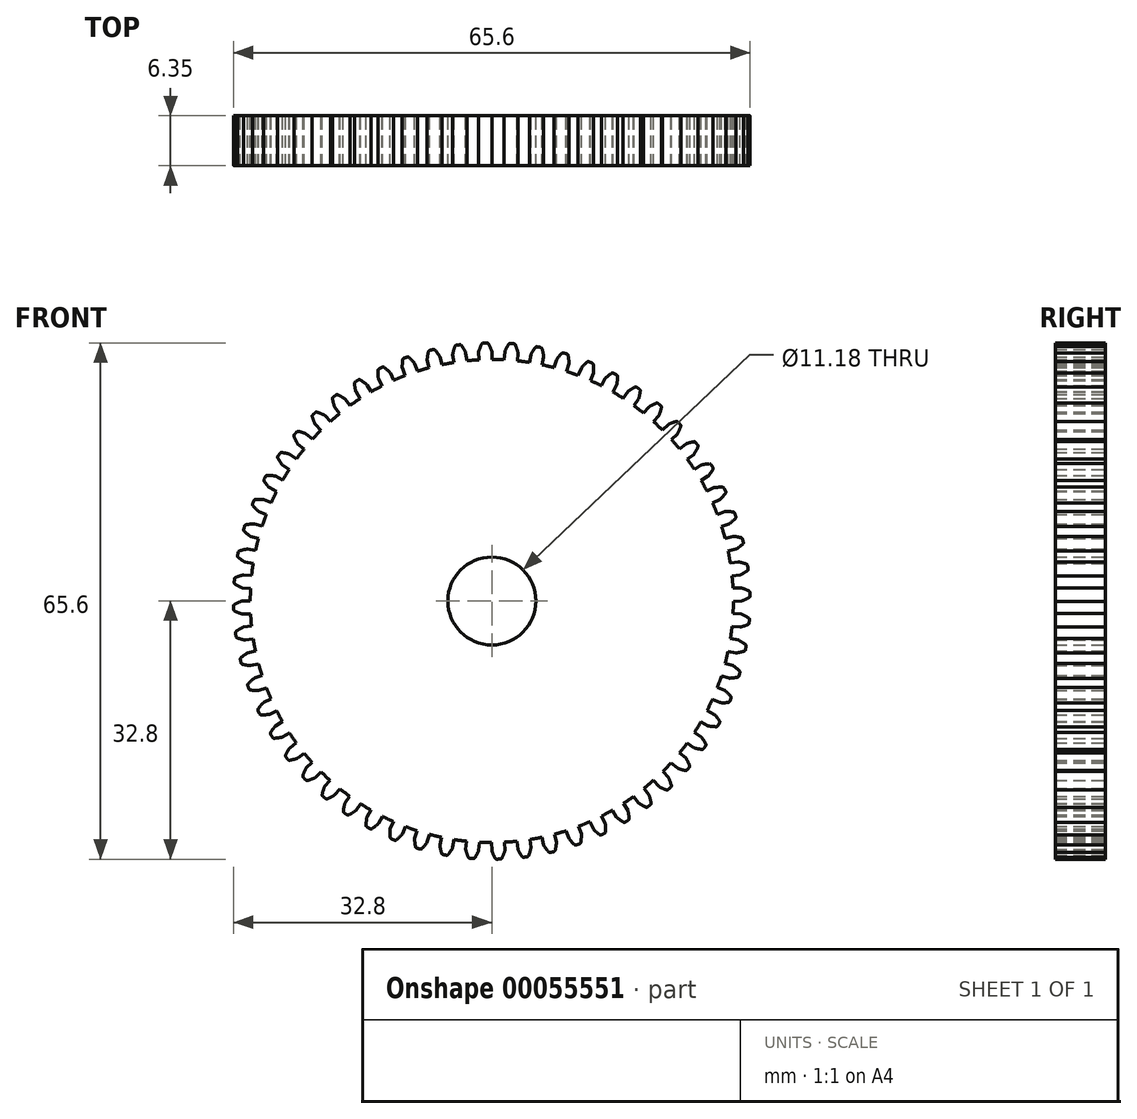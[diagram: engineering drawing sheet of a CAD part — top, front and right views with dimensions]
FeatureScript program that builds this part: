
annotation { "Feature Type Name" : "Feature", "Feature Type Description" : "" }
export const myFeature = defineFeature(function(context is Context, id is Id, definition is map)
    precondition{}
    {
        {
            var Q0;
            Q0=qCreatedBy(makeId("Front.planeOp"),FACE);
            var sketch = newSketch(context, id + "F0", { "sketchPlane" : qUnion([Q0])});
            skCircle(sketch, "E0", {"center": v(0, 0) * mm, "radius": 30.68 * mm});
            skArc(sketch, "E1", {"start": v(-0.65, 32.8) * mm, "mid": v(-0.75, 32.8) * mm, "end": v(-0.86, 32.8) * mm});
            skLineSegment(sketch, "E2", {"start": v(-1.25, 23.9) * mm, "end": v(-1.25, 23.91) * mm, "construction": true});
            skArc(sketch, "E3.trimOffspring", {"start": v(-0.02, 31.8) * mm, "mid": v(-0.2, 32.23) * mm, "end": v(-0.42, 32.66) * mm});
            skLineSegment(sketch, "E4", {"start": v(0, 31.7) * mm, "end": v(0.03, 30.68) * mm});
            skLineSegment(sketch, "E5.MirrorCS", {"start": v(-1.66, 31.66) * mm, "end": v(-1.63, 30.64) * mm});
            skArc(sketch, "E6.MirrorCS", {"start": v(-1.65, 31.75) * mm, "mid": v(-1.48, 32.2) * mm, "end": v(-1.3, 32.64) * mm});
            skArc(sketch, "E7.MirrorCS", {"start": v(-1.07, 32.79) * mm, "mid": v(-0.96, 32.79) * mm, "end": v(-0.86, 32.8) * mm});
            skPoint(sketch, "E8.visualSharp", {"position": v(-1.22, 32.78) * mm});
            skArc(sketch, "E8.filletArc", {"start": v(-1.07, 32.79) * mm, "mid": v(-1.2, 32.75) * mm, "end": v(-1.3, 32.64) * mm});
            skPoint(sketch, "E9.visualSharp", {"position": v(-0.5, 32.8) * mm});
            skArc(sketch, "E9.filletArc", {"start": v(-0.42, 32.66) * mm, "mid": v(-0.52, 32.76) * mm, "end": v(-0.65, 32.8) * mm});
            skPoint(sketch, "E10.visualSharp", {"position": v(0, 31.75) * mm});
            skArc(sketch, "E10.filletArc", {"start": v(0, 31.7) * mm, "mid": v(0, 31.75) * mm, "end": v(-0.02, 31.8) * mm});
            skPoint(sketch, "E11.visualSharp", {"position": v(-1.66, 31.7) * mm});
            skArc(sketch, "E11.filletArc", {"start": v(-1.65, 31.75) * mm, "mid": v(-1.66, 31.7) * mm, "end": v(-1.66, 31.66) * mm});
            skArc(sketch, "E12.1.0", {"start": v(-3.34, 31.62) * mm, "mid": v(-3.57, 32.04) * mm, "end": v(-3.83, 32.44) * mm});
            skArc(sketch, "E12.1.1", {"start": v(-4.96, 31.4) * mm, "mid": v(-4.84, 31.87) * mm, "end": v(-4.7, 32.33) * mm});
            skLineSegment(sketch, "E12.1.2", {"start": v(-4.96, 31.32) * mm, "end": v(-4.83, 30.3) * mm});
            skLineSegment(sketch, "E12.1.3", {"start": v(-3.31, 31.53) * mm, "end": v(-3.18, 30.52) * mm});
            skPoint(sketch, "E12.1.4", {"position": v(-3.32, 31.58) * mm});
            skPoint(sketch, "E12.1.5", {"position": v(-3.92, 32.57) * mm});
            skPoint(sketch, "E12.1.6", {"position": v(-4.64, 32.47) * mm});
            skPoint(sketch, "E12.1.7", {"position": v(-4.97, 31.36) * mm});
            skArc(sketch, "E12.1.8", {"start": v(-3.83, 32.44) * mm, "mid": v(-3.94, 32.53) * mm, "end": v(-4.07, 32.55) * mm});
            skArc(sketch, "E12.1.9", {"start": v(-4.5, 32.5) * mm, "mid": v(-4.62, 32.44) * mm, "end": v(-4.7, 32.33) * mm});
            skArc(sketch, "E12.1.10", {"start": v(-4.07, 32.55) * mm, "mid": v(-4.18, 32.54) * mm, "end": v(-4.28, 32.52) * mm});
            skArc(sketch, "E12.1.11", {"start": v(-3.31, 31.53) * mm, "mid": v(-3.32, 31.58) * mm, "end": v(-3.34, 31.62) * mm});
            skArc(sketch, "E12.1.12", {"start": v(-4.96, 31.4) * mm, "mid": v(-4.96, 31.36) * mm, "end": v(-4.96, 31.32) * mm});
            skArc(sketch, "E12.1.13", {"start": v(-4.5, 32.5) * mm, "mid": v(-4.39, 32.5) * mm, "end": v(-4.28, 32.52) * mm});
            skArc(sketch, "E12.2.0", {"start": v(-6.63, 31.1) * mm, "mid": v(-6.9, 31.49) * mm, "end": v(-7.2, 31.86) * mm});
            skArc(sketch, "E12.2.1", {"start": v(-8.21, 30.71) * mm, "mid": v(-8.14, 31.19) * mm, "end": v(-8.05, 31.66) * mm});
            skLineSegment(sketch, "E12.2.2", {"start": v(-8.2, 30.63) * mm, "end": v(-7.97, 29.63) * mm});
            skLineSegment(sketch, "E12.2.3", {"start": v(-6.6, 31.01) * mm, "end": v(-6.35, 30.02) * mm});
            skPoint(sketch, "E12.2.4", {"position": v(-6.6, 31.06) * mm});
            skPoint(sketch, "E12.2.5", {"position": v(-7.3, 31.98) * mm});
            skPoint(sketch, "E12.2.6", {"position": v(-8.01, 31.81) * mm});
            skPoint(sketch, "E12.2.7", {"position": v(-8.22, 30.67) * mm});
            skArc(sketch, "E12.2.8", {"start": v(-7.2, 31.86) * mm, "mid": v(-7.32, 31.94) * mm, "end": v(-7.45, 31.95) * mm});
            skArc(sketch, "E12.2.9", {"start": v(-7.86, 31.85) * mm, "mid": v(-7.98, 31.78) * mm, "end": v(-8.05, 31.66) * mm});
            skArc(sketch, "E12.2.10", {"start": v(-7.45, 31.95) * mm, "mid": v(-7.56, 31.92) * mm, "end": v(-7.66, 31.9) * mm});
            skArc(sketch, "E12.2.11", {"start": v(-6.6, 31.01) * mm, "mid": v(-6.6, 31.06) * mm, "end": v(-6.63, 31.1) * mm});
            skArc(sketch, "E12.2.12", {"start": v(-8.21, 30.71) * mm, "mid": v(-8.21, 30.67) * mm, "end": v(-8.2, 30.63) * mm});
            skArc(sketch, "E12.2.13", {"start": v(-7.86, 31.85) * mm, "mid": v(-7.76, 31.87) * mm, "end": v(-7.66, 31.9) * mm});
            skArc(sketch, "E12.3.0", {"start": v(-9.84, 30.23) * mm, "mid": v(-10.16, 30.6) * mm, "end": v(-10.5, 30.94) * mm});
            skArc(sketch, "E12.3.1", {"start": v(-11.38, 29.69) * mm, "mid": v(-11.36, 30.17) * mm, "end": v(-11.31, 30.65) * mm});
            skLineSegment(sketch, "E12.3.2", {"start": v(-11.36, 29.6) * mm, "end": v(-11.02, 28.64) * mm});
            skLineSegment(sketch, "E12.3.3", {"start": v(-9.8, 30.15) * mm, "end": v(-9.46, 29.2) * mm});
            skPoint(sketch, "E12.3.4", {"position": v(-9.81, 30.2) * mm});
            skPoint(sketch, "E12.3.5", {"position": v(-10.6, 31.04) * mm});
            skPoint(sketch, "E12.3.6", {"position": v(-11.3, 30.8) * mm});
            skPoint(sketch, "E12.3.7", {"position": v(-11.38, 29.64) * mm});
            skArc(sketch, "E12.3.8", {"start": v(-10.5, 30.94) * mm, "mid": v(-10.61, 31) * mm, "end": v(-10.75, 31) * mm});
            skArc(sketch, "E12.3.9", {"start": v(-11.15, 30.85) * mm, "mid": v(-11.26, 30.77) * mm, "end": v(-11.31, 30.65) * mm});
            skArc(sketch, "E12.3.10", {"start": v(-10.75, 31) * mm, "mid": v(-10.85, 30.96) * mm, "end": v(-10.95, 30.92) * mm});
            skArc(sketch, "E12.3.11", {"start": v(-9.8, 30.15) * mm, "mid": v(-9.81, 30.2) * mm, "end": v(-9.84, 30.23) * mm});
            skArc(sketch, "E12.3.12", {"start": v(-11.38, 29.69) * mm, "mid": v(-11.37, 29.64) * mm, "end": v(-11.36, 29.6) * mm});
            skArc(sketch, "E12.3.13", {"start": v(-11.15, 30.85) * mm, "mid": v(-11.05, 30.89) * mm, "end": v(-10.95, 30.92) * mm});
            skArc(sketch, "E12.4.0", {"start": v(-12.95, 29.04) * mm, "mid": v(-13.3, 29.36) * mm, "end": v(-13.67, 29.67) * mm});
            skArc(sketch, "E12.4.1", {"start": v(-14.42, 28.33) * mm, "mid": v(-14.45, 28.81) * mm, "end": v(-14.46, 29.3) * mm});
            skLineSegment(sketch, "E12.4.2", {"start": v(-14.4, 28.25) * mm, "end": v(-13.95, 27.33) * mm});
            skLineSegment(sketch, "E12.4.3", {"start": v(-12.9, 28.97) * mm, "end": v(-12.45, 28.04) * mm});
            skPoint(sketch, "E12.4.4", {"position": v(-12.91, 29) * mm});
            skPoint(sketch, "E12.4.5", {"position": v(-13.8, 29.76) * mm});
            skPoint(sketch, "E12.4.6", {"position": v(-14.45, 29.45) * mm});
            skPoint(sketch, "E12.4.7", {"position": v(-14.41, 28.29) * mm});
            skArc(sketch, "E12.4.8", {"start": v(-13.67, 29.67) * mm, "mid": v(-13.8, 29.72) * mm, "end": v(-13.93, 29.7) * mm});
            skArc(sketch, "E12.4.9", {"start": v(-14.31, 29.52) * mm, "mid": v(-14.41, 29.43) * mm, "end": v(-14.46, 29.3) * mm});
            skArc(sketch, "E12.4.10", {"start": v(-13.93, 29.7) * mm, "mid": v(-14.03, 29.65) * mm, "end": v(-14.12, 29.6) * mm});
            skArc(sketch, "E12.4.11", {"start": v(-12.9, 28.97) * mm, "mid": v(-12.92, 29) * mm, "end": v(-12.95, 29.04) * mm});
            skArc(sketch, "E12.4.12", {"start": v(-14.42, 28.33) * mm, "mid": v(-14.41, 28.3) * mm, "end": v(-14.4, 28.25) * mm});
            skArc(sketch, "E12.4.13", {"start": v(-14.31, 29.52) * mm, "mid": v(-14.22, 29.56) * mm, "end": v(-14.12, 29.6) * mm});
            skArc(sketch, "E12.5.0", {"start": v(-15.9, 27.52) * mm, "mid": v(-16.3, 27.81) * mm, "end": v(-16.7, 28.08) * mm});
            skArc(sketch, "E12.5.1", {"start": v(-17.3, 26.67) * mm, "mid": v(-17.38, 27.15) * mm, "end": v(-17.44, 27.62) * mm});
            skLineSegment(sketch, "E12.5.2", {"start": v(-17.27, 26.6) * mm, "end": v(-16.73, 25.72) * mm});
            skLineSegment(sketch, "E12.5.3", {"start": v(-15.85, 27.46) * mm, "end": v(-15.32, 26.59) * mm});
            skPoint(sketch, "E12.5.4", {"position": v(-15.87, 27.5) * mm});
            skPoint(sketch, "E12.5.5", {"position": v(-16.83, 28.16) * mm});
            skPoint(sketch, "E12.5.6", {"position": v(-17.45, 27.78) * mm});
            skPoint(sketch, "E12.5.7", {"position": v(-17.3, 26.63) * mm});
            skArc(sketch, "E12.5.8", {"start": v(-16.7, 28.08) * mm, "mid": v(-16.83, 28.12) * mm, "end": v(-16.96, 28.08) * mm});
            skArc(sketch, "E12.5.9", {"start": v(-17.32, 27.86) * mm, "mid": v(-17.41, 27.76) * mm, "end": v(-17.44, 27.62) * mm});
            skArc(sketch, "E12.5.10", {"start": v(-16.96, 28.08) * mm, "mid": v(-17.05, 28.02) * mm, "end": v(-17.14, 27.97) * mm});
            skArc(sketch, "E12.5.11", {"start": v(-15.85, 27.46) * mm, "mid": v(-15.88, 27.5) * mm, "end": v(-15.9, 27.52) * mm});
            skArc(sketch, "E12.5.12", {"start": v(-17.3, 26.67) * mm, "mid": v(-17.29, 26.63) * mm, "end": v(-17.27, 26.6) * mm});
            skArc(sketch, "E12.5.13", {"start": v(-17.32, 27.86) * mm, "mid": v(-17.23, 27.92) * mm, "end": v(-17.14, 27.97) * mm});
            skArc(sketch, "E12.6.0", {"start": v(-18.7, 25.71) * mm, "mid": v(-19.11, 25.96) * mm, "end": v(-19.54, 26.18) * mm});
            skArc(sketch, "E12.6.1", {"start": v(-20, 24.72) * mm, "mid": v(-20.13, 25.18) * mm, "end": v(-20.23, 25.65) * mm});
            skLineSegment(sketch, "E12.6.2", {"start": v(-19.95, 24.64) * mm, "end": v(-19.33, 23.83) * mm});
            skLineSegment(sketch, "E12.6.3", {"start": v(-18.64, 25.65) * mm, "end": v(-18.01, 24.84) * mm});
            skPoint(sketch, "E12.6.4", {"position": v(-18.66, 25.69) * mm});
            skPoint(sketch, "E12.6.5", {"position": v(-19.68, 26.25) * mm});
            skPoint(sketch, "E12.6.6", {"position": v(-20.26, 25.8) * mm});
            skPoint(sketch, "E12.6.7", {"position": v(-19.98, 24.67) * mm});
            skArc(sketch, "E12.6.8", {"start": v(-19.54, 26.18) * mm, "mid": v(-19.67, 26.2) * mm, "end": v(-19.8, 26.15) * mm});
            skArc(sketch, "E12.6.9", {"start": v(-20.14, 25.9) * mm, "mid": v(-20.22, 25.79) * mm, "end": v(-20.23, 25.65) * mm});
            skArc(sketch, "E12.6.10", {"start": v(-19.8, 26.15) * mm, "mid": v(-19.89, 26.09) * mm, "end": v(-19.97, 26.03) * mm});
            skArc(sketch, "E12.6.11", {"start": v(-18.64, 25.65) * mm, "mid": v(-18.67, 25.68) * mm, "end": v(-18.7, 25.71) * mm});
            skArc(sketch, "E12.6.12", {"start": v(-20, 24.72) * mm, "mid": v(-19.98, 24.68) * mm, "end": v(-19.95, 24.64) * mm});
            skArc(sketch, "E12.6.13", {"start": v(-20.14, 25.9) * mm, "mid": v(-20.05, 25.96) * mm, "end": v(-19.97, 26.03) * mm});
            skArc(sketch, "E12.7.0", {"start": v(-21.28, 23.62) * mm, "mid": v(-21.72, 23.82) * mm, "end": v(-22.17, 24) * mm});
            skArc(sketch, "E12.7.1", {"start": v(-22.47, 22.5) * mm, "mid": v(-22.65, 22.94) * mm, "end": v(-22.8, 23.4) * mm});
            skLineSegment(sketch, "E12.7.2", {"start": v(-22.42, 22.42) * mm, "end": v(-21.72, 21.68) * mm});
            skLineSegment(sketch, "E12.7.3", {"start": v(-21.21, 23.56) * mm, "end": v(-20.51, 22.82) * mm});
            skPoint(sketch, "E12.7.4", {"position": v(-21.24, 23.6) * mm});
            skPoint(sketch, "E12.7.5", {"position": v(-22.32, 24.04) * mm});
            skPoint(sketch, "E12.7.6", {"position": v(-22.84, 23.54) * mm});
            skPoint(sketch, "E12.7.7", {"position": v(-22.45, 22.45) * mm});
            skArc(sketch, "E12.7.8", {"start": v(-22.17, 24) * mm, "mid": v(-22.3, 24) * mm, "end": v(-22.43, 23.94) * mm});
            skArc(sketch, "E12.7.9", {"start": v(-22.73, 23.65) * mm, "mid": v(-22.8, 23.53) * mm, "end": v(-22.8, 23.4) * mm});
            skArc(sketch, "E12.7.10", {"start": v(-22.43, 23.94) * mm, "mid": v(-22.5, 23.87) * mm, "end": v(-22.58, 23.8) * mm});
            skArc(sketch, "E12.7.11", {"start": v(-21.21, 23.56) * mm, "mid": v(-21.25, 23.6) * mm, "end": v(-21.28, 23.62) * mm});
            skArc(sketch, "E12.7.12", {"start": v(-22.47, 22.5) * mm, "mid": v(-22.45, 22.45) * mm, "end": v(-22.42, 22.42) * mm});
            skArc(sketch, "E12.7.13", {"start": v(-22.73, 23.65) * mm, "mid": v(-22.66, 23.72) * mm, "end": v(-22.58, 23.8) * mm});
            skArc(sketch, "E12.8.0", {"start": v(-23.64, 21.26) * mm, "mid": v(-24.1, 21.42) * mm, "end": v(-24.56, 21.54) * mm});
            skArc(sketch, "E12.8.1", {"start": v(-24.7, 20.02) * mm, "mid": v(-24.92, 20.44) * mm, "end": v(-25.12, 20.88) * mm});
            skLineSegment(sketch, "E12.8.2", {"start": v(-24.64, 19.95) * mm, "end": v(-23.86, 19.29) * mm});
            skLineSegment(sketch, "E12.8.3", {"start": v(-23.56, 21.22) * mm, "end": v(-22.78, 20.55) * mm});
            skPoint(sketch, "E12.8.4", {"position": v(-23.6, 21.24) * mm});
            skPoint(sketch, "E12.8.5", {"position": v(-24.7, 21.58) * mm});
            skPoint(sketch, "E12.8.6", {"position": v(-25.18, 21.03) * mm});
            skPoint(sketch, "E12.8.7", {"position": v(-24.67, 19.98) * mm});
            skArc(sketch, "E12.8.8", {"start": v(-24.56, 21.54) * mm, "mid": v(-24.7, 21.54) * mm, "end": v(-24.8, 21.46) * mm});
            skArc(sketch, "E12.8.9", {"start": v(-25.08, 21.14) * mm, "mid": v(-25.14, 21.02) * mm, "end": v(-25.12, 20.88) * mm});
            skArc(sketch, "E12.8.10", {"start": v(-24.8, 21.46) * mm, "mid": v(-24.88, 21.38) * mm, "end": v(-24.94, 21.3) * mm});
            skArc(sketch, "E12.8.11", {"start": v(-23.56, 21.22) * mm, "mid": v(-23.6, 21.24) * mm, "end": v(-23.64, 21.26) * mm});
            skArc(sketch, "E12.8.12", {"start": v(-24.7, 20.02) * mm, "mid": v(-24.67, 19.98) * mm, "end": v(-24.64, 19.95) * mm});
            skArc(sketch, "E12.8.13", {"start": v(-25.08, 21.14) * mm, "mid": v(-25.01, 21.22) * mm, "end": v(-24.94, 21.3) * mm});
            skArc(sketch, "E12.9.0", {"start": v(-25.73, 18.67) * mm, "mid": v(-26.2, 18.78) * mm, "end": v(-26.67, 18.86) * mm});
            skArc(sketch, "E12.9.1", {"start": v(-26.65, 17.33) * mm, "mid": v(-26.92, 17.73) * mm, "end": v(-27.17, 18.14) * mm});
            skLineSegment(sketch, "E12.9.2", {"start": v(-26.6, 17.27) * mm, "end": v(-25.75, 16.69) * mm});
            skLineSegment(sketch, "E12.9.3", {"start": v(-25.65, 18.64) * mm, "end": v(-24.8, 18.06) * mm});
            skPoint(sketch, "E12.9.4", {"position": v(-25.69, 18.66) * mm});
            skPoint(sketch, "E12.9.5", {"position": v(-26.83, 18.88) * mm});
            skPoint(sketch, "E12.9.6", {"position": v(-27.24, 18.28) * mm});
            skPoint(sketch, "E12.9.7", {"position": v(-26.63, 17.3) * mm});
            skArc(sketch, "E12.9.8", {"start": v(-26.67, 18.86) * mm, "mid": v(-26.8, 18.84) * mm, "end": v(-26.92, 18.75) * mm});
            skArc(sketch, "E12.9.9", {"start": v(-27.15, 18.4) * mm, "mid": v(-27.2, 18.28) * mm, "end": v(-27.17, 18.14) * mm});
            skArc(sketch, "E12.9.10", {"start": v(-26.92, 18.75) * mm, "mid": v(-26.98, 18.67) * mm, "end": v(-27.03, 18.58) * mm});
            skArc(sketch, "E12.9.11", {"start": v(-25.65, 18.64) * mm, "mid": v(-25.69, 18.66) * mm, "end": v(-25.73, 18.67) * mm});
            skArc(sketch, "E12.9.12", {"start": v(-26.65, 17.33) * mm, "mid": v(-26.63, 17.3) * mm, "end": v(-26.6, 17.27) * mm});
            skArc(sketch, "E12.9.13", {"start": v(-27.15, 18.4) * mm, "mid": v(-27.1, 18.5) * mm, "end": v(-27.03, 18.58) * mm});
            skArc(sketch, "E12.10.0", {"start": v(-27.54, 15.88) * mm, "mid": v(-28.02, 15.94) * mm, "end": v(-28.5, 15.97) * mm});
            skArc(sketch, "E12.10.1", {"start": v(-28.32, 14.45) * mm, "mid": v(-28.63, 14.82) * mm, "end": v(-28.91, 15.2) * mm});
            skLineSegment(sketch, "E12.10.2", {"start": v(-28.25, 14.4) * mm, "end": v(-27.35, 13.9) * mm});
            skLineSegment(sketch, "E12.10.3", {"start": v(-27.46, 15.85) * mm, "end": v(-26.56, 15.37) * mm});
            skPoint(sketch, "E12.10.4", {"position": v(-27.5, 15.88) * mm});
            skPoint(sketch, "E12.10.5", {"position": v(-28.65, 15.97) * mm});
            skPoint(sketch, "E12.10.6", {"position": v(-29, 15.33) * mm});
            skPoint(sketch, "E12.10.7", {"position": v(-28.29, 14.41) * mm});
            skArc(sketch, "E12.10.8", {"start": v(-28.5, 15.97) * mm, "mid": v(-28.63, 15.94) * mm, "end": v(-28.73, 15.84) * mm});
            skArc(sketch, "E12.10.9", {"start": v(-28.93, 15.47) * mm, "mid": v(-28.96, 15.33) * mm, "end": v(-28.91, 15.2) * mm});
            skArc(sketch, "E12.10.10", {"start": v(-28.73, 15.84) * mm, "mid": v(-28.78, 15.75) * mm, "end": v(-28.83, 15.65) * mm});
            skArc(sketch, "E12.10.11", {"start": v(-27.46, 15.85) * mm, "mid": v(-27.5, 15.87) * mm, "end": v(-27.54, 15.88) * mm});
            skArc(sketch, "E12.10.12", {"start": v(-28.32, 14.45) * mm, "mid": v(-28.29, 14.42) * mm, "end": v(-28.25, 14.4) * mm});
            skArc(sketch, "E12.10.13", {"start": v(-28.93, 15.47) * mm, "mid": v(-28.88, 15.56) * mm, "end": v(-28.83, 15.65) * mm});
            skArc(sketch, "E12.11.0", {"start": v(-29.05, 12.92) * mm, "mid": v(-29.53, 12.92) * mm, "end": v(-30.01, 12.9) * mm});
            skArc(sketch, "E12.11.1", {"start": v(-29.67, 11.4) * mm, "mid": v(-30.02, 11.74) * mm, "end": v(-30.34, 12.1) * mm});
            skLineSegment(sketch, "E12.11.2", {"start": v(-29.6, 11.36) * mm, "end": v(-28.66, 10.97) * mm});
            skLineSegment(sketch, "E12.11.3", {"start": v(-28.96, 12.9) * mm, "end": v(-28.02, 12.5) * mm});
            skPoint(sketch, "E12.11.4", {"position": v(-29, 12.91) * mm});
            skPoint(sketch, "E12.11.5", {"position": v(-30.17, 12.89) * mm});
            skPoint(sketch, "E12.11.6", {"position": v(-30.44, 12.22) * mm});
            skPoint(sketch, "E12.11.7", {"position": v(-29.64, 11.38) * mm});
            skArc(sketch, "E12.11.8", {"start": v(-30.01, 12.9) * mm, "mid": v(-30.14, 12.86) * mm, "end": v(-30.23, 12.75) * mm});
            skArc(sketch, "E12.11.9", {"start": v(-30.39, 12.36) * mm, "mid": v(-30.4, 12.22) * mm, "end": v(-30.34, 12.1) * mm});
            skArc(sketch, "E12.11.10", {"start": v(-30.23, 12.75) * mm, "mid": v(-30.27, 12.65) * mm, "end": v(-30.3, 12.55) * mm});
            skArc(sketch, "E12.11.11", {"start": v(-28.96, 12.9) * mm, "mid": v(-29, 12.91) * mm, "end": v(-29.05, 12.92) * mm});
            skArc(sketch, "E12.11.12", {"start": v(-29.67, 11.4) * mm, "mid": v(-29.64, 11.38) * mm, "end": v(-29.6, 11.36) * mm});
            skArc(sketch, "E12.11.13", {"start": v(-30.39, 12.36) * mm, "mid": v(-30.35, 12.46) * mm, "end": v(-30.3, 12.55) * mm});
            skArc(sketch, "E12.12.0", {"start": v(-30.24, 9.8) * mm, "mid": v(-30.72, 9.77) * mm, "end": v(-31.2, 9.7) * mm});
            skArc(sketch, "E12.12.1", {"start": v(-30.7, 8.24) * mm, "mid": v(-31.08, 8.54) * mm, "end": v(-31.44, 8.86) * mm});
            skLineSegment(sketch, "E12.12.2", {"start": v(-30.63, 8.2) * mm, "end": v(-29.64, 7.91) * mm});
            skLineSegment(sketch, "E12.12.3", {"start": v(-30.15, 9.8) * mm, "end": v(-29.17, 9.5) * mm});
            skPoint(sketch, "E12.12.4", {"position": v(-30.2, 9.81) * mm});
            skPoint(sketch, "E12.12.5", {"position": v(-31.35, 9.67) * mm});
            skPoint(sketch, "E12.12.6", {"position": v(-31.55, 8.97) * mm});
            skPoint(sketch, "E12.12.7", {"position": v(-30.67, 8.22) * mm});
            skArc(sketch, "E12.12.8", {"start": v(-31.2, 9.7) * mm, "mid": v(-31.32, 9.63) * mm, "end": v(-31.4, 9.52) * mm});
            skArc(sketch, "E12.12.9", {"start": v(-31.51, 9.12) * mm, "mid": v(-31.51, 8.98) * mm, "end": v(-31.44, 8.86) * mm});
            skArc(sketch, "E12.12.10", {"start": v(-31.4, 9.52) * mm, "mid": v(-31.42, 9.42) * mm, "end": v(-31.45, 9.32) * mm});
            skArc(sketch, "E12.12.11", {"start": v(-30.15, 9.8) * mm, "mid": v(-30.2, 9.8) * mm, "end": v(-30.24, 9.8) * mm});
            skArc(sketch, "E12.12.12", {"start": v(-30.7, 8.24) * mm, "mid": v(-30.67, 8.22) * mm, "end": v(-30.63, 8.2) * mm});
            skArc(sketch, "E12.12.13", {"start": v(-31.51, 9.12) * mm, "mid": v(-31.48, 9.22) * mm, "end": v(-31.45, 9.32) * mm});
            skArc(sketch, "E12.13.0", {"start": v(-31.1, 6.6) * mm, "mid": v(-31.57, 6.5) * mm, "end": v(-32.04, 6.38) * mm});
            skArc(sketch, "E12.13.1", {"start": v(-31.4, 4.99) * mm, "mid": v(-31.8, 5.24) * mm, "end": v(-32.2, 5.52) * mm});
            skLineSegment(sketch, "E12.13.2", {"start": v(-31.32, 4.96) * mm, "end": v(-30.3, 4.77) * mm});
            skLineSegment(sketch, "E12.13.3", {"start": v(-31.01, 6.6) * mm, "end": v(-30, 6.4) * mm});
            skPoint(sketch, "E12.13.4", {"position": v(-31.06, 6.6) * mm});
            skPoint(sketch, "E12.13.5", {"position": v(-32.19, 6.34) * mm});
            skPoint(sketch, "E12.13.6", {"position": v(-32.32, 5.62) * mm});
            skPoint(sketch, "E12.13.7", {"position": v(-31.36, 4.97) * mm});
            skArc(sketch, "E12.13.8", {"start": v(-32.04, 6.38) * mm, "mid": v(-32.15, 6.3) * mm, "end": v(-32.22, 6.18) * mm});
            skArc(sketch, "E12.13.9", {"start": v(-32.3, 5.77) * mm, "mid": v(-32.28, 5.63) * mm, "end": v(-32.2, 5.52) * mm});
            skArc(sketch, "E12.13.10", {"start": v(-32.22, 6.18) * mm, "mid": v(-32.24, 6.08) * mm, "end": v(-32.25, 5.98) * mm});
            skArc(sketch, "E12.13.11", {"start": v(-31.01, 6.6) * mm, "mid": v(-31.06, 6.6) * mm, "end": v(-31.1, 6.6) * mm});
            skArc(sketch, "E12.13.12", {"start": v(-31.4, 4.99) * mm, "mid": v(-31.36, 4.97) * mm, "end": v(-31.32, 4.96) * mm});
            skArc(sketch, "E12.13.13", {"start": v(-32.3, 5.77) * mm, "mid": v(-32.27, 5.87) * mm, "end": v(-32.25, 5.98) * mm});
            skArc(sketch, "E12.14.0", {"start": v(-31.62, 3.3) * mm, "mid": v(-32.08, 3.17) * mm, "end": v(-32.53, 3) * mm});
            skArc(sketch, "E12.14.1", {"start": v(-31.75, 1.68) * mm, "mid": v(-32.18, 1.9) * mm, "end": v(-32.6, 2.13) * mm});
            skLineSegment(sketch, "E12.14.2", {"start": v(-31.66, 1.66) * mm, "end": v(-30.64, 1.58) * mm});
            skLineSegment(sketch, "E12.14.3", {"start": v(-31.53, 3.32) * mm, "end": v(-30.51, 3.24) * mm});
            skPoint(sketch, "E12.14.4", {"position": v(-31.58, 3.32) * mm});
            skPoint(sketch, "E12.14.5", {"position": v(-32.67, 2.94) * mm});
            skPoint(sketch, "E12.14.6", {"position": v(-32.73, 2.21) * mm});
            skPoint(sketch, "E12.14.7", {"position": v(-31.7, 1.66) * mm});
            skArc(sketch, "E12.14.8", {"start": v(-32.53, 3) * mm, "mid": v(-32.64, 2.91) * mm, "end": v(-32.69, 2.78) * mm});
            skArc(sketch, "E12.14.9", {"start": v(-32.72, 2.36) * mm, "mid": v(-32.7, 2.23) * mm, "end": v(-32.6, 2.13) * mm});
            skArc(sketch, "E12.14.10", {"start": v(-32.69, 2.78) * mm, "mid": v(-32.7, 2.68) * mm, "end": v(-32.7, 2.57) * mm});
            skArc(sketch, "E12.14.11", {"start": v(-31.53, 3.32) * mm, "mid": v(-31.58, 3.31) * mm, "end": v(-31.62, 3.3) * mm});
            skArc(sketch, "E12.14.12", {"start": v(-31.75, 1.68) * mm, "mid": v(-31.7, 1.67) * mm, "end": v(-31.66, 1.66) * mm});
            skArc(sketch, "E12.14.13", {"start": v(-32.72, 2.36) * mm, "mid": v(-32.71, 2.47) * mm, "end": v(-32.7, 2.57) * mm});
            skArc(sketch, "E12.15.0", {"start": v(-31.8, -0.02) * mm, "mid": v(-32.23, -0.2) * mm, "end": v(-32.66, -0.42) * mm});
            skArc(sketch, "E12.15.1", {"start": v(-31.75, -1.65) * mm, "mid": v(-32.2, -1.48) * mm, "end": v(-32.64, -1.3) * mm});
            skLineSegment(sketch, "E12.15.2", {"start": v(-31.66, -1.66) * mm, "end": v(-30.64, -1.63) * mm});
            skLineSegment(sketch, "E12.15.3", {"start": v(-31.7, 0) * mm, "end": v(-30.68, 0.03) * mm});
            skPoint(sketch, "E12.15.4", {"position": v(-31.75, 0) * mm});
            skPoint(sketch, "E12.15.5", {"position": v(-32.8, -0.5) * mm});
            skPoint(sketch, "E12.15.6", {"position": v(-32.78, -1.22) * mm});
            skPoint(sketch, "E12.15.7", {"position": v(-31.7, -1.66) * mm});
            skArc(sketch, "E12.15.8", {"start": v(-32.66, -0.42) * mm, "mid": v(-32.76, -0.52) * mm, "end": v(-32.8, -0.65) * mm});
            skArc(sketch, "E12.15.9", {"start": v(-32.79, -1.07) * mm, "mid": v(-32.75, -1.2) * mm, "end": v(-32.64, -1.3) * mm});
            skArc(sketch, "E12.15.10", {"start": v(-32.8, -0.65) * mm, "mid": v(-32.8, -0.75) * mm, "end": v(-32.8, -0.86) * mm});
            skArc(sketch, "E12.15.11", {"start": v(-31.7, 0) * mm, "mid": v(-31.75, 0) * mm, "end": v(-31.8, -0.02) * mm});
            skArc(sketch, "E12.15.12", {"start": v(-31.75, -1.65) * mm, "mid": v(-31.7, -1.66) * mm, "end": v(-31.66, -1.66) * mm});
            skArc(sketch, "E12.15.13", {"start": v(-32.79, -1.07) * mm, "mid": v(-32.79, -0.96) * mm, "end": v(-32.8, -0.86) * mm});
            skArc(sketch, "E12.16.0", {"start": v(-31.62, -3.34) * mm, "mid": v(-32.04, -3.57) * mm, "end": v(-32.44, -3.83) * mm});
            skArc(sketch, "E12.16.1", {"start": v(-31.4, -4.96) * mm, "mid": v(-31.87, -4.84) * mm, "end": v(-32.33, -4.7) * mm});
            skLineSegment(sketch, "E12.16.2", {"start": v(-31.32, -4.96) * mm, "end": v(-30.3, -4.83) * mm});
            skLineSegment(sketch, "E12.16.3", {"start": v(-31.53, -3.31) * mm, "end": v(-30.52, -3.18) * mm});
            skPoint(sketch, "E12.16.4", {"position": v(-31.58, -3.32) * mm});
            skPoint(sketch, "E12.16.5", {"position": v(-32.57, -3.92) * mm});
            skPoint(sketch, "E12.16.6", {"position": v(-32.47, -4.64) * mm});
            skPoint(sketch, "E12.16.7", {"position": v(-31.36, -4.97) * mm});
            skArc(sketch, "E12.16.8", {"start": v(-32.44, -3.83) * mm, "mid": v(-32.53, -3.94) * mm, "end": v(-32.55, -4.07) * mm});
            skArc(sketch, "E12.16.9", {"start": v(-32.5, -4.5) * mm, "mid": v(-32.44, -4.62) * mm, "end": v(-32.33, -4.7) * mm});
            skArc(sketch, "E12.16.10", {"start": v(-32.55, -4.07) * mm, "mid": v(-32.54, -4.18) * mm, "end": v(-32.52, -4.28) * mm});
            skArc(sketch, "E12.16.11", {"start": v(-31.53, -3.31) * mm, "mid": v(-31.58, -3.32) * mm, "end": v(-31.62, -3.34) * mm});
            skArc(sketch, "E12.16.12", {"start": v(-31.4, -4.96) * mm, "mid": v(-31.36, -4.96) * mm, "end": v(-31.32, -4.96) * mm});
            skArc(sketch, "E12.16.13", {"start": v(-32.5, -4.5) * mm, "mid": v(-32.5, -4.39) * mm, "end": v(-32.52, -4.28) * mm});
            skArc(sketch, "E12.17.0", {"start": v(-31.1, -6.63) * mm, "mid": v(-31.49, -6.9) * mm, "end": v(-31.86, -7.2) * mm});
            skArc(sketch, "E12.17.1", {"start": v(-30.71, -8.21) * mm, "mid": v(-31.19, -8.14) * mm, "end": v(-31.66, -8.05) * mm});
            skLineSegment(sketch, "E12.17.2", {"start": v(-30.63, -8.2) * mm, "end": v(-29.63, -7.97) * mm});
            skLineSegment(sketch, "E12.17.3", {"start": v(-31.01, -6.6) * mm, "end": v(-30.02, -6.35) * mm});
            skPoint(sketch, "E12.17.4", {"position": v(-31.06, -6.6) * mm});
            skPoint(sketch, "E12.17.5", {"position": v(-31.98, -7.3) * mm});
            skPoint(sketch, "E12.17.6", {"position": v(-31.81, -8.01) * mm});
            skPoint(sketch, "E12.17.7", {"position": v(-30.67, -8.22) * mm});
            skArc(sketch, "E12.17.8", {"start": v(-31.86, -7.2) * mm, "mid": v(-31.94, -7.32) * mm, "end": v(-31.95, -7.45) * mm});
            skArc(sketch, "E12.17.9", {"start": v(-31.85, -7.86) * mm, "mid": v(-31.78, -7.98) * mm, "end": v(-31.66, -8.05) * mm});
            skArc(sketch, "E12.17.10", {"start": v(-31.95, -7.45) * mm, "mid": v(-31.92, -7.56) * mm, "end": v(-31.9, -7.66) * mm});
            skArc(sketch, "E12.17.11", {"start": v(-31.01, -6.6) * mm, "mid": v(-31.06, -6.6) * mm, "end": v(-31.1, -6.63) * mm});
            skArc(sketch, "E12.17.12", {"start": v(-30.71, -8.21) * mm, "mid": v(-30.67, -8.21) * mm, "end": v(-30.63, -8.2) * mm});
            skArc(sketch, "E12.17.13", {"start": v(-31.85, -7.86) * mm, "mid": v(-31.87, -7.76) * mm, "end": v(-31.9, -7.66) * mm});
            skArc(sketch, "E12.18.0", {"start": v(-30.23, -9.84) * mm, "mid": v(-30.6, -10.16) * mm, "end": v(-30.94, -10.5) * mm});
            skArc(sketch, "E12.18.1", {"start": v(-29.69, -11.38) * mm, "mid": v(-30.17, -11.36) * mm, "end": v(-30.65, -11.31) * mm});
            skLineSegment(sketch, "E12.18.2", {"start": v(-29.6, -11.36) * mm, "end": v(-28.64, -11.02) * mm});
            skLineSegment(sketch, "E12.18.3", {"start": v(-30.15, -9.8) * mm, "end": v(-29.2, -9.46) * mm});
            skPoint(sketch, "E12.18.4", {"position": v(-30.2, -9.81) * mm});
            skPoint(sketch, "E12.18.5", {"position": v(-31.04, -10.6) * mm});
            skPoint(sketch, "E12.18.6", {"position": v(-30.8, -11.3) * mm});
            skPoint(sketch, "E12.18.7", {"position": v(-29.64, -11.38) * mm});
            skArc(sketch, "E12.18.8", {"start": v(-30.94, -10.5) * mm, "mid": v(-31, -10.61) * mm, "end": v(-31, -10.75) * mm});
            skArc(sketch, "E12.18.9", {"start": v(-30.85, -11.15) * mm, "mid": v(-30.77, -11.26) * mm, "end": v(-30.65, -11.31) * mm});
            skArc(sketch, "E12.18.10", {"start": v(-31, -10.75) * mm, "mid": v(-30.96, -10.85) * mm, "end": v(-30.92, -10.95) * mm});
            skArc(sketch, "E12.18.11", {"start": v(-30.15, -9.8) * mm, "mid": v(-30.2, -9.81) * mm, "end": v(-30.23, -9.84) * mm});
            skArc(sketch, "E12.18.12", {"start": v(-29.69, -11.38) * mm, "mid": v(-29.64, -11.37) * mm, "end": v(-29.6, -11.36) * mm});
            skArc(sketch, "E12.18.13", {"start": v(-30.85, -11.15) * mm, "mid": v(-30.89, -11.05) * mm, "end": v(-30.92, -10.95) * mm});
            skArc(sketch, "E12.19.0", {"start": v(-29.04, -12.95) * mm, "mid": v(-29.36, -13.3) * mm, "end": v(-29.67, -13.67) * mm});
            skArc(sketch, "E12.19.1", {"start": v(-28.33, -14.42) * mm, "mid": v(-28.81, -14.45) * mm, "end": v(-29.3, -14.46) * mm});
            skLineSegment(sketch, "E12.19.2", {"start": v(-28.25, -14.4) * mm, "end": v(-27.33, -13.95) * mm});
            skLineSegment(sketch, "E12.19.3", {"start": v(-28.97, -12.9) * mm, "end": v(-28.04, -12.45) * mm});
            skPoint(sketch, "E12.19.4", {"position": v(-29, -12.91) * mm});
            skPoint(sketch, "E12.19.5", {"position": v(-29.76, -13.8) * mm});
            skPoint(sketch, "E12.19.6", {"position": v(-29.45, -14.45) * mm});
            skPoint(sketch, "E12.19.7", {"position": v(-28.29, -14.41) * mm});
            skArc(sketch, "E12.19.8", {"start": v(-29.67, -13.67) * mm, "mid": v(-29.72, -13.8) * mm, "end": v(-29.7, -13.93) * mm});
            skArc(sketch, "E12.19.9", {"start": v(-29.52, -14.31) * mm, "mid": v(-29.43, -14.41) * mm, "end": v(-29.3, -14.46) * mm});
            skArc(sketch, "E12.19.10", {"start": v(-29.7, -13.93) * mm, "mid": v(-29.65, -14.03) * mm, "end": v(-29.6, -14.12) * mm});
            skArc(sketch, "E12.19.11", {"start": v(-28.97, -12.9) * mm, "mid": v(-29, -12.92) * mm, "end": v(-29.04, -12.95) * mm});
            skArc(sketch, "E12.19.12", {"start": v(-28.33, -14.42) * mm, "mid": v(-28.3, -14.41) * mm, "end": v(-28.25, -14.4) * mm});
            skArc(sketch, "E12.19.13", {"start": v(-29.52, -14.31) * mm, "mid": v(-29.56, -14.22) * mm, "end": v(-29.6, -14.12) * mm});
            skArc(sketch, "E12.20.0", {"start": v(-27.52, -15.9) * mm, "mid": v(-27.81, -16.3) * mm, "end": v(-28.08, -16.7) * mm});
            skArc(sketch, "E12.20.1", {"start": v(-26.67, -17.3) * mm, "mid": v(-27.15, -17.38) * mm, "end": v(-27.62, -17.44) * mm});
            skLineSegment(sketch, "E12.20.2", {"start": v(-26.6, -17.27) * mm, "end": v(-25.72, -16.73) * mm});
            skLineSegment(sketch, "E12.20.3", {"start": v(-27.46, -15.85) * mm, "end": v(-26.59, -15.32) * mm});
            skPoint(sketch, "E12.20.4", {"position": v(-27.5, -15.87) * mm});
            skPoint(sketch, "E12.20.5", {"position": v(-28.16, -16.83) * mm});
            skPoint(sketch, "E12.20.6", {"position": v(-27.78, -17.45) * mm});
            skPoint(sketch, "E12.20.7", {"position": v(-26.63, -17.3) * mm});
            skArc(sketch, "E12.20.8", {"start": v(-28.08, -16.7) * mm, "mid": v(-28.12, -16.83) * mm, "end": v(-28.08, -16.96) * mm});
            skArc(sketch, "E12.20.9", {"start": v(-27.86, -17.32) * mm, "mid": v(-27.76, -17.41) * mm, "end": v(-27.62, -17.44) * mm});
            skArc(sketch, "E12.20.10", {"start": v(-28.08, -16.96) * mm, "mid": v(-28.02, -17.05) * mm, "end": v(-27.97, -17.14) * mm});
            skArc(sketch, "E12.20.11", {"start": v(-27.46, -15.85) * mm, "mid": v(-27.5, -15.88) * mm, "end": v(-27.52, -15.9) * mm});
            skArc(sketch, "E12.20.12", {"start": v(-26.67, -17.3) * mm, "mid": v(-26.63, -17.29) * mm, "end": v(-26.6, -17.27) * mm});
            skArc(sketch, "E12.20.13", {"start": v(-27.86, -17.32) * mm, "mid": v(-27.92, -17.23) * mm, "end": v(-27.97, -17.14) * mm});
            skArc(sketch, "E12.21.0", {"start": v(-25.71, -18.7) * mm, "mid": v(-25.96, -19.11) * mm, "end": v(-26.18, -19.54) * mm});
            skArc(sketch, "E12.21.1", {"start": v(-24.72, -20) * mm, "mid": v(-25.18, -20.13) * mm, "end": v(-25.65, -20.23) * mm});
            skLineSegment(sketch, "E12.21.2", {"start": v(-24.64, -19.95) * mm, "end": v(-23.83, -19.33) * mm});
            skLineSegment(sketch, "E12.21.3", {"start": v(-25.65, -18.64) * mm, "end": v(-24.84, -18.01) * mm});
            skPoint(sketch, "E12.21.4", {"position": v(-25.69, -18.66) * mm});
            skPoint(sketch, "E12.21.5", {"position": v(-26.25, -19.68) * mm});
            skPoint(sketch, "E12.21.6", {"position": v(-25.8, -20.26) * mm});
            skPoint(sketch, "E12.21.7", {"position": v(-24.67, -19.98) * mm});
            skArc(sketch, "E12.21.8", {"start": v(-26.18, -19.54) * mm, "mid": v(-26.2, -19.67) * mm, "end": v(-26.15, -19.8) * mm});
            skArc(sketch, "E12.21.9", {"start": v(-25.9, -20.14) * mm, "mid": v(-25.79, -20.22) * mm, "end": v(-25.65, -20.23) * mm});
            skArc(sketch, "E12.21.10", {"start": v(-26.15, -19.8) * mm, "mid": v(-26.09, -19.89) * mm, "end": v(-26.03, -19.97) * mm});
            skArc(sketch, "E12.21.11", {"start": v(-25.65, -18.64) * mm, "mid": v(-25.68, -18.67) * mm, "end": v(-25.71, -18.7) * mm});
            skArc(sketch, "E12.21.12", {"start": v(-24.72, -20) * mm, "mid": v(-24.68, -19.98) * mm, "end": v(-24.64, -19.95) * mm});
            skArc(sketch, "E12.21.13", {"start": v(-25.9, -20.14) * mm, "mid": v(-25.96, -20.05) * mm, "end": v(-26.03, -19.97) * mm});
            skArc(sketch, "E12.22.0", {"start": v(-23.62, -21.28) * mm, "mid": v(-23.82, -21.72) * mm, "end": v(-24, -22.17) * mm});
            skArc(sketch, "E12.22.1", {"start": v(-22.5, -22.47) * mm, "mid": v(-22.94, -22.65) * mm, "end": v(-23.4, -22.8) * mm});
            skLineSegment(sketch, "E12.22.2", {"start": v(-22.42, -22.42) * mm, "end": v(-21.68, -21.72) * mm});
            skLineSegment(sketch, "E12.22.3", {"start": v(-23.56, -21.21) * mm, "end": v(-22.82, -20.51) * mm});
            skPoint(sketch, "E12.22.4", {"position": v(-23.6, -21.24) * mm});
            skPoint(sketch, "E12.22.5", {"position": v(-24.04, -22.32) * mm});
            skPoint(sketch, "E12.22.6", {"position": v(-23.54, -22.84) * mm});
            skPoint(sketch, "E12.22.7", {"position": v(-22.45, -22.45) * mm});
            skArc(sketch, "E12.22.8", {"start": v(-24, -22.17) * mm, "mid": v(-24, -22.3) * mm, "end": v(-23.94, -22.43) * mm});
            skArc(sketch, "E12.22.9", {"start": v(-23.65, -22.73) * mm, "mid": v(-23.53, -22.8) * mm, "end": v(-23.4, -22.8) * mm});
            skArc(sketch, "E12.22.10", {"start": v(-23.94, -22.43) * mm, "mid": v(-23.87, -22.5) * mm, "end": v(-23.8, -22.58) * mm});
            skArc(sketch, "E12.22.11", {"start": v(-23.56, -21.21) * mm, "mid": v(-23.6, -21.25) * mm, "end": v(-23.62, -21.28) * mm});
            skArc(sketch, "E12.22.12", {"start": v(-22.5, -22.47) * mm, "mid": v(-22.45, -22.45) * mm, "end": v(-22.42, -22.42) * mm});
            skArc(sketch, "E12.22.13", {"start": v(-23.65, -22.73) * mm, "mid": v(-23.72, -22.66) * mm, "end": v(-23.8, -22.58) * mm});
            skArc(sketch, "E12.23.0", {"start": v(-21.26, -23.64) * mm, "mid": v(-21.42, -24.1) * mm, "end": v(-21.54, -24.56) * mm});
            skArc(sketch, "E12.23.1", {"start": v(-20.02, -24.7) * mm, "mid": v(-20.44, -24.92) * mm, "end": v(-20.88, -25.12) * mm});
            skLineSegment(sketch, "E12.23.2", {"start": v(-19.95, -24.64) * mm, "end": v(-19.29, -23.86) * mm});
            skLineSegment(sketch, "E12.23.3", {"start": v(-21.22, -23.56) * mm, "end": v(-20.55, -22.78) * mm});
            skPoint(sketch, "E12.23.4", {"position": v(-21.24, -23.6) * mm});
            skPoint(sketch, "E12.23.5", {"position": v(-21.58, -24.7) * mm});
            skPoint(sketch, "E12.23.6", {"position": v(-21.03, -25.18) * mm});
            skPoint(sketch, "E12.23.7", {"position": v(-19.98, -24.67) * mm});
            skArc(sketch, "E12.23.8", {"start": v(-21.54, -24.56) * mm, "mid": v(-21.54, -24.7) * mm, "end": v(-21.46, -24.8) * mm});
            skArc(sketch, "E12.23.9", {"start": v(-21.14, -25.08) * mm, "mid": v(-21.02, -25.14) * mm, "end": v(-20.88, -25.12) * mm});
            skArc(sketch, "E12.23.10", {"start": v(-21.46, -24.8) * mm, "mid": v(-21.38, -24.88) * mm, "end": v(-21.3, -24.94) * mm});
            skArc(sketch, "E12.23.11", {"start": v(-21.22, -23.56) * mm, "mid": v(-21.24, -23.6) * mm, "end": v(-21.26, -23.64) * mm});
            skArc(sketch, "E12.23.12", {"start": v(-20.02, -24.7) * mm, "mid": v(-19.98, -24.67) * mm, "end": v(-19.95, -24.64) * mm});
            skArc(sketch, "E12.23.13", {"start": v(-21.14, -25.08) * mm, "mid": v(-21.22, -25.01) * mm, "end": v(-21.3, -24.94) * mm});
            skArc(sketch, "E12.24.0", {"start": v(-18.67, -25.73) * mm, "mid": v(-18.78, -26.2) * mm, "end": v(-18.86, -26.67) * mm});
            skArc(sketch, "E12.24.1", {"start": v(-17.33, -26.65) * mm, "mid": v(-17.73, -26.92) * mm, "end": v(-18.14, -27.17) * mm});
            skLineSegment(sketch, "E12.24.2", {"start": v(-17.27, -26.6) * mm, "end": v(-16.69, -25.75) * mm});
            skLineSegment(sketch, "E12.24.3", {"start": v(-18.64, -25.65) * mm, "end": v(-18.06, -24.8) * mm});
            skPoint(sketch, "E12.24.4", {"position": v(-18.66, -25.69) * mm});
            skPoint(sketch, "E12.24.5", {"position": v(-18.88, -26.83) * mm});
            skPoint(sketch, "E12.24.6", {"position": v(-18.28, -27.24) * mm});
            skPoint(sketch, "E12.24.7", {"position": v(-17.3, -26.63) * mm});
            skArc(sketch, "E12.24.8", {"start": v(-18.86, -26.67) * mm, "mid": v(-18.84, -26.8) * mm, "end": v(-18.75, -26.92) * mm});
            skArc(sketch, "E12.24.9", {"start": v(-18.4, -27.15) * mm, "mid": v(-18.28, -27.2) * mm, "end": v(-18.14, -27.17) * mm});
            skArc(sketch, "E12.24.10", {"start": v(-18.75, -26.92) * mm, "mid": v(-18.67, -26.98) * mm, "end": v(-18.58, -27.03) * mm});
            skArc(sketch, "E12.24.11", {"start": v(-18.64, -25.65) * mm, "mid": v(-18.66, -25.69) * mm, "end": v(-18.67, -25.73) * mm});
            skArc(sketch, "E12.24.12", {"start": v(-17.33, -26.65) * mm, "mid": v(-17.3, -26.63) * mm, "end": v(-17.27, -26.6) * mm});
            skArc(sketch, "E12.24.13", {"start": v(-18.4, -27.15) * mm, "mid": v(-18.5, -27.1) * mm, "end": v(-18.58, -27.03) * mm});
            skArc(sketch, "E12.25.0", {"start": v(-15.88, -27.54) * mm, "mid": v(-15.94, -28.02) * mm, "end": v(-15.97, -28.5) * mm});
            skArc(sketch, "E12.25.1", {"start": v(-14.45, -28.32) * mm, "mid": v(-14.82, -28.63) * mm, "end": v(-15.2, -28.91) * mm});
            skLineSegment(sketch, "E12.25.2", {"start": v(-14.4, -28.25) * mm, "end": v(-13.9, -27.35) * mm});
            skLineSegment(sketch, "E12.25.3", {"start": v(-15.85, -27.46) * mm, "end": v(-15.37, -26.56) * mm});
            skPoint(sketch, "E12.25.4", {"position": v(-15.87, -27.5) * mm});
            skPoint(sketch, "E12.25.5", {"position": v(-15.97, -28.65) * mm});
            skPoint(sketch, "E12.25.6", {"position": v(-15.33, -29) * mm});
            skPoint(sketch, "E12.25.7", {"position": v(-14.41, -28.29) * mm});
            skArc(sketch, "E12.25.8", {"start": v(-15.97, -28.5) * mm, "mid": v(-15.94, -28.63) * mm, "end": v(-15.84, -28.73) * mm});
            skArc(sketch, "E12.25.9", {"start": v(-15.47, -28.93) * mm, "mid": v(-15.33, -28.96) * mm, "end": v(-15.2, -28.91) * mm});
            skArc(sketch, "E12.25.10", {"start": v(-15.84, -28.73) * mm, "mid": v(-15.75, -28.78) * mm, "end": v(-15.65, -28.83) * mm});
            skArc(sketch, "E12.25.11", {"start": v(-15.85, -27.46) * mm, "mid": v(-15.87, -27.5) * mm, "end": v(-15.88, -27.54) * mm});
            skArc(sketch, "E12.25.12", {"start": v(-14.45, -28.32) * mm, "mid": v(-14.42, -28.29) * mm, "end": v(-14.4, -28.25) * mm});
            skArc(sketch, "E12.25.13", {"start": v(-15.47, -28.93) * mm, "mid": v(-15.56, -28.88) * mm, "end": v(-15.65, -28.83) * mm});
            skArc(sketch, "E12.26.0", {"start": v(-12.92, -29.05) * mm, "mid": v(-12.92, -29.53) * mm, "end": v(-12.9, -30.01) * mm});
            skArc(sketch, "E12.26.1", {"start": v(-11.4, -29.67) * mm, "mid": v(-11.74, -30.02) * mm, "end": v(-12.1, -30.34) * mm});
            skLineSegment(sketch, "E12.26.2", {"start": v(-11.36, -29.6) * mm, "end": v(-10.97, -28.66) * mm});
            skLineSegment(sketch, "E12.26.3", {"start": v(-12.9, -28.96) * mm, "end": v(-12.5, -28.02) * mm});
            skPoint(sketch, "E12.26.4", {"position": v(-12.91, -29) * mm});
            skPoint(sketch, "E12.26.5", {"position": v(-12.89, -30.17) * mm});
            skPoint(sketch, "E12.26.6", {"position": v(-12.22, -30.44) * mm});
            skPoint(sketch, "E12.26.7", {"position": v(-11.38, -29.64) * mm});
            skArc(sketch, "E12.26.8", {"start": v(-12.9, -30.01) * mm, "mid": v(-12.86, -30.14) * mm, "end": v(-12.75, -30.23) * mm});
            skArc(sketch, "E12.26.9", {"start": v(-12.36, -30.39) * mm, "mid": v(-12.22, -30.4) * mm, "end": v(-12.1, -30.34) * mm});
            skArc(sketch, "E12.26.10", {"start": v(-12.75, -30.23) * mm, "mid": v(-12.65, -30.27) * mm, "end": v(-12.55, -30.3) * mm});
            skArc(sketch, "E12.26.11", {"start": v(-12.9, -28.96) * mm, "mid": v(-12.91, -29) * mm, "end": v(-12.92, -29.05) * mm});
            skArc(sketch, "E12.26.12", {"start": v(-11.4, -29.67) * mm, "mid": v(-11.38, -29.64) * mm, "end": v(-11.36, -29.6) * mm});
            skArc(sketch, "E12.26.13", {"start": v(-12.36, -30.39) * mm, "mid": v(-12.46, -30.35) * mm, "end": v(-12.55, -30.3) * mm});
            skArc(sketch, "E12.27.0", {"start": v(-9.8, -30.24) * mm, "mid": v(-9.77, -30.72) * mm, "end": v(-9.7, -31.2) * mm});
            skArc(sketch, "E12.27.1", {"start": v(-8.24, -30.7) * mm, "mid": v(-8.54, -31.08) * mm, "end": v(-8.86, -31.44) * mm});
            skLineSegment(sketch, "E12.27.2", {"start": v(-8.2, -30.63) * mm, "end": v(-7.91, -29.64) * mm});
            skLineSegment(sketch, "E12.27.3", {"start": v(-9.8, -30.15) * mm, "end": v(-9.5, -29.17) * mm});
            skPoint(sketch, "E12.27.4", {"position": v(-9.81, -30.2) * mm});
            skPoint(sketch, "E12.27.5", {"position": v(-9.67, -31.35) * mm});
            skPoint(sketch, "E12.27.6", {"position": v(-8.97, -31.55) * mm});
            skPoint(sketch, "E12.27.7", {"position": v(-8.22, -30.67) * mm});
            skArc(sketch, "E12.27.8", {"start": v(-9.7, -31.2) * mm, "mid": v(-9.63, -31.32) * mm, "end": v(-9.52, -31.4) * mm});
            skArc(sketch, "E12.27.9", {"start": v(-9.12, -31.51) * mm, "mid": v(-8.98, -31.51) * mm, "end": v(-8.86, -31.44) * mm});
            skArc(sketch, "E12.27.10", {"start": v(-9.52, -31.4) * mm, "mid": v(-9.42, -31.42) * mm, "end": v(-9.32, -31.45) * mm});
            skArc(sketch, "E12.27.11", {"start": v(-9.8, -30.15) * mm, "mid": v(-9.8, -30.2) * mm, "end": v(-9.8, -30.24) * mm});
            skArc(sketch, "E12.27.12", {"start": v(-8.24, -30.7) * mm, "mid": v(-8.22, -30.67) * mm, "end": v(-8.2, -30.63) * mm});
            skArc(sketch, "E12.27.13", {"start": v(-9.12, -31.51) * mm, "mid": v(-9.22, -31.48) * mm, "end": v(-9.32, -31.45) * mm});
            skArc(sketch, "E12.28.0", {"start": v(-6.6, -31.1) * mm, "mid": v(-6.5, -31.57) * mm, "end": v(-6.38, -32.04) * mm});
            skArc(sketch, "E12.28.1", {"start": v(-4.99, -31.4) * mm, "mid": v(-5.24, -31.8) * mm, "end": v(-5.52, -32.2) * mm});
            skLineSegment(sketch, "E12.28.2", {"start": v(-4.96, -31.32) * mm, "end": v(-4.77, -30.3) * mm});
            skLineSegment(sketch, "E12.28.3", {"start": v(-6.6, -31.01) * mm, "end": v(-6.4, -30) * mm});
            skPoint(sketch, "E12.28.4", {"position": v(-6.6, -31.06) * mm});
            skPoint(sketch, "E12.28.5", {"position": v(-6.34, -32.19) * mm});
            skPoint(sketch, "E12.28.6", {"position": v(-5.62, -32.32) * mm});
            skPoint(sketch, "E12.28.7", {"position": v(-4.97, -31.36) * mm});
            skArc(sketch, "E12.28.8", {"start": v(-6.38, -32.04) * mm, "mid": v(-6.3, -32.15) * mm, "end": v(-6.18, -32.22) * mm});
            skArc(sketch, "E12.28.9", {"start": v(-5.77, -32.3) * mm, "mid": v(-5.63, -32.28) * mm, "end": v(-5.52, -32.2) * mm});
            skArc(sketch, "E12.28.10", {"start": v(-6.18, -32.22) * mm, "mid": v(-6.08, -32.24) * mm, "end": v(-5.98, -32.25) * mm});
            skArc(sketch, "E12.28.11", {"start": v(-6.6, -31.01) * mm, "mid": v(-6.6, -31.06) * mm, "end": v(-6.6, -31.1) * mm});
            skArc(sketch, "E12.28.12", {"start": v(-4.99, -31.4) * mm, "mid": v(-4.97, -31.36) * mm, "end": v(-4.96, -31.32) * mm});
            skArc(sketch, "E12.28.13", {"start": v(-5.77, -32.3) * mm, "mid": v(-5.87, -32.27) * mm, "end": v(-5.98, -32.25) * mm});
            skArc(sketch, "E12.29.0", {"start": v(-3.3, -31.62) * mm, "mid": v(-3.17, -32.08) * mm, "end": v(-3, -32.53) * mm});
            skArc(sketch, "E12.29.1", {"start": v(-1.68, -31.75) * mm, "mid": v(-1.9, -32.18) * mm, "end": v(-2.13, -32.6) * mm});
            skLineSegment(sketch, "E12.29.2", {"start": v(-1.66, -31.66) * mm, "end": v(-1.58, -30.64) * mm});
            skLineSegment(sketch, "E12.29.3", {"start": v(-3.32, -31.53) * mm, "end": v(-3.24, -30.51) * mm});
            skPoint(sketch, "E12.29.4", {"position": v(-3.32, -31.58) * mm});
            skPoint(sketch, "E12.29.5", {"position": v(-2.94, -32.67) * mm});
            skPoint(sketch, "E12.29.6", {"position": v(-2.21, -32.73) * mm});
            skPoint(sketch, "E12.29.7", {"position": v(-1.66, -31.7) * mm});
            skArc(sketch, "E12.29.8", {"start": v(-3, -32.53) * mm, "mid": v(-2.91, -32.64) * mm, "end": v(-2.78, -32.69) * mm});
            skArc(sketch, "E12.29.9", {"start": v(-2.36, -32.72) * mm, "mid": v(-2.23, -32.7) * mm, "end": v(-2.13, -32.6) * mm});
            skArc(sketch, "E12.29.10", {"start": v(-2.78, -32.69) * mm, "mid": v(-2.68, -32.7) * mm, "end": v(-2.57, -32.7) * mm});
            skArc(sketch, "E12.29.11", {"start": v(-3.32, -31.53) * mm, "mid": v(-3.31, -31.58) * mm, "end": v(-3.3, -31.62) * mm});
            skArc(sketch, "E12.29.12", {"start": v(-1.68, -31.75) * mm, "mid": v(-1.67, -31.7) * mm, "end": v(-1.66, -31.66) * mm});
            skArc(sketch, "E12.29.13", {"start": v(-2.36, -32.72) * mm, "mid": v(-2.47, -32.71) * mm, "end": v(-2.57, -32.7) * mm});
            skArc(sketch, "E12.30.0", {"start": v(0.02, -31.8) * mm, "mid": v(0.2, -32.23) * mm, "end": v(0.42, -32.66) * mm});
            skArc(sketch, "E12.30.1", {"start": v(1.65, -31.75) * mm, "mid": v(1.48, -32.2) * mm, "end": v(1.3, -32.64) * mm});
            skLineSegment(sketch, "E12.30.2", {"start": v(1.66, -31.66) * mm, "end": v(1.63, -30.64) * mm});
            skLineSegment(sketch, "E12.30.3", {"start": v(0, -31.7) * mm, "end": v(-0.03, -30.68) * mm});
            skPoint(sketch, "E12.30.4", {"position": v(0, -31.75) * mm});
            skPoint(sketch, "E12.30.5", {"position": v(0.5, -32.8) * mm});
            skPoint(sketch, "E12.30.6", {"position": v(1.22, -32.78) * mm});
            skPoint(sketch, "E12.30.7", {"position": v(1.66, -31.7) * mm});
            skArc(sketch, "E12.30.8", {"start": v(0.42, -32.66) * mm, "mid": v(0.52, -32.76) * mm, "end": v(0.65, -32.8) * mm});
            skArc(sketch, "E12.30.9", {"start": v(1.07, -32.79) * mm, "mid": v(1.2, -32.75) * mm, "end": v(1.3, -32.64) * mm});
            skArc(sketch, "E12.30.10", {"start": v(0.65, -32.8) * mm, "mid": v(0.75, -32.8) * mm, "end": v(0.86, -32.8) * mm});
            skArc(sketch, "E12.30.11", {"start": v(0, -31.7) * mm, "mid": v(0, -31.75) * mm, "end": v(0.02, -31.8) * mm});
            skArc(sketch, "E12.30.12", {"start": v(1.65, -31.75) * mm, "mid": v(1.66, -31.7) * mm, "end": v(1.66, -31.66) * mm});
            skArc(sketch, "E12.30.13", {"start": v(1.07, -32.79) * mm, "mid": v(0.96, -32.79) * mm, "end": v(0.86, -32.8) * mm});
            skArc(sketch, "E12.31.0", {"start": v(3.34, -31.62) * mm, "mid": v(3.57, -32.04) * mm, "end": v(3.83, -32.44) * mm});
            skArc(sketch, "E12.31.1", {"start": v(4.96, -31.4) * mm, "mid": v(4.84, -31.87) * mm, "end": v(4.7, -32.33) * mm});
            skLineSegment(sketch, "E12.31.2", {"start": v(4.96, -31.32) * mm, "end": v(4.83, -30.3) * mm});
            skLineSegment(sketch, "E12.31.3", {"start": v(3.31, -31.53) * mm, "end": v(3.18, -30.52) * mm});
            skPoint(sketch, "E12.31.4", {"position": v(3.32, -31.58) * mm});
            skPoint(sketch, "E12.31.5", {"position": v(3.92, -32.57) * mm});
            skPoint(sketch, "E12.31.6", {"position": v(4.64, -32.47) * mm});
            skPoint(sketch, "E12.31.7", {"position": v(4.97, -31.36) * mm});
            skArc(sketch, "E12.31.8", {"start": v(3.83, -32.44) * mm, "mid": v(3.94, -32.53) * mm, "end": v(4.07, -32.55) * mm});
            skArc(sketch, "E12.31.9", {"start": v(4.5, -32.5) * mm, "mid": v(4.62, -32.44) * mm, "end": v(4.7, -32.33) * mm});
            skArc(sketch, "E12.31.10", {"start": v(4.07, -32.55) * mm, "mid": v(4.18, -32.54) * mm, "end": v(4.28, -32.52) * mm});
            skArc(sketch, "E12.31.11", {"start": v(3.31, -31.53) * mm, "mid": v(3.32, -31.58) * mm, "end": v(3.34, -31.62) * mm});
            skArc(sketch, "E12.31.12", {"start": v(4.96, -31.4) * mm, "mid": v(4.96, -31.36) * mm, "end": v(4.96, -31.32) * mm});
            skArc(sketch, "E12.31.13", {"start": v(4.5, -32.5) * mm, "mid": v(4.39, -32.5) * mm, "end": v(4.28, -32.52) * mm});
            skArc(sketch, "E12.32.0", {"start": v(6.63, -31.1) * mm, "mid": v(6.9, -31.49) * mm, "end": v(7.2, -31.86) * mm});
            skArc(sketch, "E12.32.1", {"start": v(8.21, -30.71) * mm, "mid": v(8.14, -31.19) * mm, "end": v(8.05, -31.66) * mm});
            skLineSegment(sketch, "E12.32.2", {"start": v(8.2, -30.63) * mm, "end": v(7.97, -29.63) * mm});
            skLineSegment(sketch, "E12.32.3", {"start": v(6.6, -31.01) * mm, "end": v(6.35, -30.02) * mm});
            skPoint(sketch, "E12.32.4", {"position": v(6.6, -31.06) * mm});
            skPoint(sketch, "E12.32.5", {"position": v(7.3, -31.98) * mm});
            skPoint(sketch, "E12.32.6", {"position": v(8.01, -31.81) * mm});
            skPoint(sketch, "E12.32.7", {"position": v(8.22, -30.67) * mm});
            skArc(sketch, "E12.32.8", {"start": v(7.2, -31.86) * mm, "mid": v(7.32, -31.94) * mm, "end": v(7.45, -31.95) * mm});
            skArc(sketch, "E12.32.9", {"start": v(7.86, -31.85) * mm, "mid": v(7.98, -31.78) * mm, "end": v(8.05, -31.66) * mm});
            skArc(sketch, "E12.32.10", {"start": v(7.45, -31.95) * mm, "mid": v(7.56, -31.92) * mm, "end": v(7.66, -31.9) * mm});
            skArc(sketch, "E12.32.11", {"start": v(6.6, -31.01) * mm, "mid": v(6.6, -31.06) * mm, "end": v(6.63, -31.1) * mm});
            skArc(sketch, "E12.32.12", {"start": v(8.21, -30.71) * mm, "mid": v(8.21, -30.67) * mm, "end": v(8.2, -30.63) * mm});
            skArc(sketch, "E12.32.13", {"start": v(7.86, -31.85) * mm, "mid": v(7.76, -31.87) * mm, "end": v(7.66, -31.9) * mm});
            skArc(sketch, "E12.33.0", {"start": v(9.84, -30.23) * mm, "mid": v(10.16, -30.6) * mm, "end": v(10.5, -30.94) * mm});
            skArc(sketch, "E12.33.1", {"start": v(11.38, -29.69) * mm, "mid": v(11.36, -30.17) * mm, "end": v(11.31, -30.65) * mm});
            skLineSegment(sketch, "E12.33.2", {"start": v(11.36, -29.6) * mm, "end": v(11.02, -28.64) * mm});
            skLineSegment(sketch, "E12.33.3", {"start": v(9.8, -30.15) * mm, "end": v(9.46, -29.2) * mm});
            skPoint(sketch, "E12.33.4", {"position": v(9.81, -30.2) * mm});
            skPoint(sketch, "E12.33.5", {"position": v(10.6, -31.04) * mm});
            skPoint(sketch, "E12.33.6", {"position": v(11.3, -30.8) * mm});
            skPoint(sketch, "E12.33.7", {"position": v(11.38, -29.64) * mm});
            skArc(sketch, "E12.33.8", {"start": v(10.5, -30.94) * mm, "mid": v(10.61, -31) * mm, "end": v(10.75, -31) * mm});
            skArc(sketch, "E12.33.9", {"start": v(11.15, -30.85) * mm, "mid": v(11.26, -30.77) * mm, "end": v(11.31, -30.65) * mm});
            skArc(sketch, "E12.33.10", {"start": v(10.75, -31) * mm, "mid": v(10.85, -30.96) * mm, "end": v(10.95, -30.92) * mm});
            skArc(sketch, "E12.33.11", {"start": v(9.8, -30.15) * mm, "mid": v(9.81, -30.2) * mm, "end": v(9.84, -30.23) * mm});
            skArc(sketch, "E12.33.12", {"start": v(11.38, -29.69) * mm, "mid": v(11.37, -29.64) * mm, "end": v(11.36, -29.6) * mm});
            skArc(sketch, "E12.33.13", {"start": v(11.15, -30.85) * mm, "mid": v(11.05, -30.89) * mm, "end": v(10.95, -30.92) * mm});
            skArc(sketch, "E12.34.0", {"start": v(12.95, -29.04) * mm, "mid": v(13.3, -29.36) * mm, "end": v(13.67, -29.67) * mm});
            skArc(sketch, "E12.34.1", {"start": v(14.42, -28.33) * mm, "mid": v(14.45, -28.81) * mm, "end": v(14.46, -29.3) * mm});
            skLineSegment(sketch, "E12.34.2", {"start": v(14.4, -28.25) * mm, "end": v(13.95, -27.33) * mm});
            skLineSegment(sketch, "E12.34.3", {"start": v(12.9, -28.97) * mm, "end": v(12.45, -28.04) * mm});
            skPoint(sketch, "E12.34.4", {"position": v(12.91, -29) * mm});
            skPoint(sketch, "E12.34.5", {"position": v(13.8, -29.76) * mm});
            skPoint(sketch, "E12.34.6", {"position": v(14.45, -29.45) * mm});
            skPoint(sketch, "E12.34.7", {"position": v(14.41, -28.29) * mm});
            skArc(sketch, "E12.34.8", {"start": v(13.67, -29.67) * mm, "mid": v(13.8, -29.72) * mm, "end": v(13.93, -29.7) * mm});
            skArc(sketch, "E12.34.9", {"start": v(14.31, -29.52) * mm, "mid": v(14.41, -29.43) * mm, "end": v(14.46, -29.3) * mm});
            skArc(sketch, "E12.34.10", {"start": v(13.93, -29.7) * mm, "mid": v(14.03, -29.65) * mm, "end": v(14.12, -29.6) * mm});
            skArc(sketch, "E12.34.11", {"start": v(12.9, -28.97) * mm, "mid": v(12.92, -29) * mm, "end": v(12.95, -29.04) * mm});
            skArc(sketch, "E12.34.12", {"start": v(14.42, -28.33) * mm, "mid": v(14.41, -28.3) * mm, "end": v(14.4, -28.25) * mm});
            skArc(sketch, "E12.34.13", {"start": v(14.31, -29.52) * mm, "mid": v(14.22, -29.56) * mm, "end": v(14.12, -29.6) * mm});
            skArc(sketch, "E12.35.0", {"start": v(15.9, -27.52) * mm, "mid": v(16.3, -27.81) * mm, "end": v(16.7, -28.08) * mm});
            skArc(sketch, "E12.35.1", {"start": v(17.3, -26.67) * mm, "mid": v(17.38, -27.15) * mm, "end": v(17.44, -27.62) * mm});
            skLineSegment(sketch, "E12.35.2", {"start": v(17.27, -26.6) * mm, "end": v(16.73, -25.72) * mm});
            skLineSegment(sketch, "E12.35.3", {"start": v(15.85, -27.46) * mm, "end": v(15.32, -26.59) * mm});
            skPoint(sketch, "E12.35.4", {"position": v(15.87, -27.5) * mm});
            skPoint(sketch, "E12.35.5", {"position": v(16.83, -28.16) * mm});
            skPoint(sketch, "E12.35.6", {"position": v(17.45, -27.78) * mm});
            skPoint(sketch, "E12.35.7", {"position": v(17.3, -26.63) * mm});
            skArc(sketch, "E12.35.8", {"start": v(16.7, -28.08) * mm, "mid": v(16.83, -28.12) * mm, "end": v(16.96, -28.08) * mm});
            skArc(sketch, "E12.35.9", {"start": v(17.32, -27.86) * mm, "mid": v(17.41, -27.76) * mm, "end": v(17.44, -27.62) * mm});
            skArc(sketch, "E12.35.10", {"start": v(16.96, -28.08) * mm, "mid": v(17.05, -28.02) * mm, "end": v(17.14, -27.97) * mm});
            skArc(sketch, "E12.35.11", {"start": v(15.85, -27.46) * mm, "mid": v(15.88, -27.5) * mm, "end": v(15.9, -27.52) * mm});
            skArc(sketch, "E12.35.12", {"start": v(17.3, -26.67) * mm, "mid": v(17.29, -26.63) * mm, "end": v(17.27, -26.6) * mm});
            skArc(sketch, "E12.35.13", {"start": v(17.32, -27.86) * mm, "mid": v(17.23, -27.92) * mm, "end": v(17.14, -27.97) * mm});
            skArc(sketch, "E12.36.0", {"start": v(18.7, -25.71) * mm, "mid": v(19.11, -25.96) * mm, "end": v(19.54, -26.18) * mm});
            skArc(sketch, "E12.36.1", {"start": v(20, -24.72) * mm, "mid": v(20.13, -25.18) * mm, "end": v(20.23, -25.65) * mm});
            skLineSegment(sketch, "E12.36.2", {"start": v(19.95, -24.64) * mm, "end": v(19.33, -23.83) * mm});
            skLineSegment(sketch, "E12.36.3", {"start": v(18.64, -25.65) * mm, "end": v(18.01, -24.84) * mm});
            skPoint(sketch, "E12.36.4", {"position": v(18.66, -25.69) * mm});
            skPoint(sketch, "E12.36.5", {"position": v(19.68, -26.25) * mm});
            skPoint(sketch, "E12.36.6", {"position": v(20.26, -25.8) * mm});
            skPoint(sketch, "E12.36.7", {"position": v(19.98, -24.67) * mm});
            skArc(sketch, "E12.36.8", {"start": v(19.54, -26.18) * mm, "mid": v(19.67, -26.2) * mm, "end": v(19.8, -26.15) * mm});
            skArc(sketch, "E12.36.9", {"start": v(20.14, -25.9) * mm, "mid": v(20.22, -25.79) * mm, "end": v(20.23, -25.65) * mm});
            skArc(sketch, "E12.36.10", {"start": v(19.8, -26.15) * mm, "mid": v(19.89, -26.09) * mm, "end": v(19.97, -26.03) * mm});
            skArc(sketch, "E12.36.11", {"start": v(18.64, -25.65) * mm, "mid": v(18.67, -25.68) * mm, "end": v(18.7, -25.71) * mm});
            skArc(sketch, "E12.36.12", {"start": v(20, -24.72) * mm, "mid": v(19.98, -24.68) * mm, "end": v(19.95, -24.64) * mm});
            skArc(sketch, "E12.36.13", {"start": v(20.14, -25.9) * mm, "mid": v(20.05, -25.96) * mm, "end": v(19.97, -26.03) * mm});
            skArc(sketch, "E12.37.0", {"start": v(21.28, -23.62) * mm, "mid": v(21.72, -23.82) * mm, "end": v(22.17, -24) * mm});
            skArc(sketch, "E12.37.1", {"start": v(22.47, -22.5) * mm, "mid": v(22.65, -22.94) * mm, "end": v(22.8, -23.4) * mm});
            skLineSegment(sketch, "E12.37.2", {"start": v(22.42, -22.42) * mm, "end": v(21.72, -21.68) * mm});
            skLineSegment(sketch, "E12.37.3", {"start": v(21.21, -23.56) * mm, "end": v(20.51, -22.82) * mm});
            skPoint(sketch, "E12.37.4", {"position": v(21.24, -23.6) * mm});
            skPoint(sketch, "E12.37.5", {"position": v(22.32, -24.04) * mm});
            skPoint(sketch, "E12.37.6", {"position": v(22.84, -23.54) * mm});
            skPoint(sketch, "E12.37.7", {"position": v(22.45, -22.45) * mm});
            skArc(sketch, "E12.37.8", {"start": v(22.17, -24) * mm, "mid": v(22.3, -24) * mm, "end": v(22.43, -23.94) * mm});
            skArc(sketch, "E12.37.9", {"start": v(22.73, -23.65) * mm, "mid": v(22.8, -23.53) * mm, "end": v(22.8, -23.4) * mm});
            skArc(sketch, "E12.37.10", {"start": v(22.43, -23.94) * mm, "mid": v(22.5, -23.87) * mm, "end": v(22.58, -23.8) * mm});
            skArc(sketch, "E12.37.11", {"start": v(21.21, -23.56) * mm, "mid": v(21.25, -23.6) * mm, "end": v(21.28, -23.62) * mm});
            skArc(sketch, "E12.37.12", {"start": v(22.47, -22.5) * mm, "mid": v(22.45, -22.45) * mm, "end": v(22.42, -22.42) * mm});
            skArc(sketch, "E12.37.13", {"start": v(22.73, -23.65) * mm, "mid": v(22.66, -23.72) * mm, "end": v(22.58, -23.8) * mm});
            skArc(sketch, "E12.38.0", {"start": v(23.64, -21.26) * mm, "mid": v(24.1, -21.42) * mm, "end": v(24.56, -21.54) * mm});
            skArc(sketch, "E12.38.1", {"start": v(24.7, -20.02) * mm, "mid": v(24.92, -20.44) * mm, "end": v(25.12, -20.88) * mm});
            skLineSegment(sketch, "E12.38.2", {"start": v(24.64, -19.95) * mm, "end": v(23.86, -19.29) * mm});
            skLineSegment(sketch, "E12.38.3", {"start": v(23.56, -21.22) * mm, "end": v(22.78, -20.55) * mm});
            skPoint(sketch, "E12.38.4", {"position": v(23.6, -21.24) * mm});
            skPoint(sketch, "E12.38.5", {"position": v(24.7, -21.58) * mm});
            skPoint(sketch, "E12.38.6", {"position": v(25.18, -21.03) * mm});
            skPoint(sketch, "E12.38.7", {"position": v(24.67, -19.98) * mm});
            skArc(sketch, "E12.38.8", {"start": v(24.56, -21.54) * mm, "mid": v(24.7, -21.54) * mm, "end": v(24.8, -21.46) * mm});
            skArc(sketch, "E12.38.9", {"start": v(25.08, -21.14) * mm, "mid": v(25.14, -21.02) * mm, "end": v(25.12, -20.88) * mm});
            skArc(sketch, "E12.38.10", {"start": v(24.8, -21.46) * mm, "mid": v(24.88, -21.38) * mm, "end": v(24.94, -21.3) * mm});
            skArc(sketch, "E12.38.11", {"start": v(23.56, -21.22) * mm, "mid": v(23.6, -21.24) * mm, "end": v(23.64, -21.26) * mm});
            skArc(sketch, "E12.38.12", {"start": v(24.7, -20.02) * mm, "mid": v(24.67, -19.98) * mm, "end": v(24.64, -19.95) * mm});
            skArc(sketch, "E12.38.13", {"start": v(25.08, -21.14) * mm, "mid": v(25.01, -21.22) * mm, "end": v(24.94, -21.3) * mm});
            skArc(sketch, "E12.39.0", {"start": v(25.73, -18.67) * mm, "mid": v(26.2, -18.78) * mm, "end": v(26.67, -18.86) * mm});
            skArc(sketch, "E12.39.1", {"start": v(26.65, -17.33) * mm, "mid": v(26.92, -17.73) * mm, "end": v(27.17, -18.14) * mm});
            skLineSegment(sketch, "E12.39.2", {"start": v(26.6, -17.27) * mm, "end": v(25.75, -16.69) * mm});
            skLineSegment(sketch, "E12.39.3", {"start": v(25.65, -18.64) * mm, "end": v(24.8, -18.06) * mm});
            skPoint(sketch, "E12.39.4", {"position": v(25.69, -18.66) * mm});
            skPoint(sketch, "E12.39.5", {"position": v(26.83, -18.88) * mm});
            skPoint(sketch, "E12.39.6", {"position": v(27.24, -18.28) * mm});
            skPoint(sketch, "E12.39.7", {"position": v(26.63, -17.3) * mm});
            skArc(sketch, "E12.39.8", {"start": v(26.67, -18.86) * mm, "mid": v(26.8, -18.84) * mm, "end": v(26.92, -18.75) * mm});
            skArc(sketch, "E12.39.9", {"start": v(27.15, -18.4) * mm, "mid": v(27.2, -18.28) * mm, "end": v(27.17, -18.14) * mm});
            skArc(sketch, "E12.39.10", {"start": v(26.92, -18.75) * mm, "mid": v(26.98, -18.67) * mm, "end": v(27.03, -18.58) * mm});
            skArc(sketch, "E12.39.11", {"start": v(25.65, -18.64) * mm, "mid": v(25.69, -18.66) * mm, "end": v(25.73, -18.67) * mm});
            skArc(sketch, "E12.39.12", {"start": v(26.65, -17.33) * mm, "mid": v(26.63, -17.3) * mm, "end": v(26.6, -17.27) * mm});
            skArc(sketch, "E12.39.13", {"start": v(27.15, -18.4) * mm, "mid": v(27.1, -18.5) * mm, "end": v(27.03, -18.58) * mm});
            skArc(sketch, "E12.40.0", {"start": v(27.54, -15.88) * mm, "mid": v(28.02, -15.94) * mm, "end": v(28.5, -15.97) * mm});
            skArc(sketch, "E12.40.1", {"start": v(28.32, -14.45) * mm, "mid": v(28.63, -14.82) * mm, "end": v(28.91, -15.2) * mm});
            skLineSegment(sketch, "E12.40.2", {"start": v(28.25, -14.4) * mm, "end": v(27.35, -13.9) * mm});
            skLineSegment(sketch, "E12.40.3", {"start": v(27.46, -15.85) * mm, "end": v(26.56, -15.37) * mm});
            skPoint(sketch, "E12.40.4", {"position": v(27.5, -15.88) * mm});
            skPoint(sketch, "E12.40.5", {"position": v(28.65, -15.97) * mm});
            skPoint(sketch, "E12.40.6", {"position": v(29, -15.33) * mm});
            skPoint(sketch, "E12.40.7", {"position": v(28.29, -14.41) * mm});
            skArc(sketch, "E12.40.8", {"start": v(28.5, -15.97) * mm, "mid": v(28.63, -15.94) * mm, "end": v(28.73, -15.84) * mm});
            skArc(sketch, "E12.40.9", {"start": v(28.93, -15.47) * mm, "mid": v(28.96, -15.33) * mm, "end": v(28.91, -15.2) * mm});
            skArc(sketch, "E12.40.10", {"start": v(28.73, -15.84) * mm, "mid": v(28.78, -15.75) * mm, "end": v(28.83, -15.65) * mm});
            skArc(sketch, "E12.40.11", {"start": v(27.46, -15.85) * mm, "mid": v(27.5, -15.87) * mm, "end": v(27.54, -15.88) * mm});
            skArc(sketch, "E12.40.12", {"start": v(28.32, -14.45) * mm, "mid": v(28.29, -14.42) * mm, "end": v(28.25, -14.4) * mm});
            skArc(sketch, "E12.40.13", {"start": v(28.93, -15.47) * mm, "mid": v(28.88, -15.56) * mm, "end": v(28.83, -15.65) * mm});
            skArc(sketch, "E12.41.0", {"start": v(29.05, -12.92) * mm, "mid": v(29.53, -12.92) * mm, "end": v(30.01, -12.9) * mm});
            skArc(sketch, "E12.41.1", {"start": v(29.67, -11.4) * mm, "mid": v(30.02, -11.74) * mm, "end": v(30.34, -12.1) * mm});
            skLineSegment(sketch, "E12.41.2", {"start": v(29.6, -11.36) * mm, "end": v(28.66, -10.97) * mm});
            skLineSegment(sketch, "E12.41.3", {"start": v(28.96, -12.9) * mm, "end": v(28.02, -12.5) * mm});
            skPoint(sketch, "E12.41.4", {"position": v(29, -12.91) * mm});
            skPoint(sketch, "E12.41.5", {"position": v(30.17, -12.89) * mm});
            skPoint(sketch, "E12.41.6", {"position": v(30.44, -12.22) * mm});
            skPoint(sketch, "E12.41.7", {"position": v(29.64, -11.38) * mm});
            skArc(sketch, "E12.41.8", {"start": v(30.01, -12.9) * mm, "mid": v(30.14, -12.86) * mm, "end": v(30.23, -12.75) * mm});
            skArc(sketch, "E12.41.9", {"start": v(30.39, -12.36) * mm, "mid": v(30.4, -12.22) * mm, "end": v(30.34, -12.1) * mm});
            skArc(sketch, "E12.41.10", {"start": v(30.23, -12.75) * mm, "mid": v(30.27, -12.65) * mm, "end": v(30.3, -12.55) * mm});
            skArc(sketch, "E12.41.11", {"start": v(28.96, -12.9) * mm, "mid": v(29, -12.91) * mm, "end": v(29.05, -12.92) * mm});
            skArc(sketch, "E12.41.12", {"start": v(29.67, -11.4) * mm, "mid": v(29.64, -11.38) * mm, "end": v(29.6, -11.36) * mm});
            skArc(sketch, "E12.41.13", {"start": v(30.39, -12.36) * mm, "mid": v(30.35, -12.46) * mm, "end": v(30.3, -12.55) * mm});
            skArc(sketch, "E12.42.0", {"start": v(30.24, -9.8) * mm, "mid": v(30.72, -9.77) * mm, "end": v(31.2, -9.7) * mm});
            skArc(sketch, "E12.42.1", {"start": v(30.7, -8.24) * mm, "mid": v(31.08, -8.54) * mm, "end": v(31.44, -8.86) * mm});
            skLineSegment(sketch, "E12.42.2", {"start": v(30.63, -8.2) * mm, "end": v(29.64, -7.91) * mm});
            skLineSegment(sketch, "E12.42.3", {"start": v(30.15, -9.8) * mm, "end": v(29.17, -9.5) * mm});
            skPoint(sketch, "E12.42.4", {"position": v(30.2, -9.81) * mm});
            skPoint(sketch, "E12.42.5", {"position": v(31.35, -9.67) * mm});
            skPoint(sketch, "E12.42.6", {"position": v(31.55, -8.97) * mm});
            skPoint(sketch, "E12.42.7", {"position": v(30.67, -8.22) * mm});
            skArc(sketch, "E12.42.8", {"start": v(31.2, -9.7) * mm, "mid": v(31.32, -9.63) * mm, "end": v(31.4, -9.52) * mm});
            skArc(sketch, "E12.42.9", {"start": v(31.51, -9.12) * mm, "mid": v(31.51, -8.98) * mm, "end": v(31.44, -8.86) * mm});
            skArc(sketch, "E12.42.10", {"start": v(31.4, -9.52) * mm, "mid": v(31.42, -9.42) * mm, "end": v(31.45, -9.32) * mm});
            skArc(sketch, "E12.42.11", {"start": v(30.15, -9.8) * mm, "mid": v(30.2, -9.8) * mm, "end": v(30.24, -9.8) * mm});
            skArc(sketch, "E12.42.12", {"start": v(30.7, -8.24) * mm, "mid": v(30.67, -8.22) * mm, "end": v(30.63, -8.2) * mm});
            skArc(sketch, "E12.42.13", {"start": v(31.51, -9.12) * mm, "mid": v(31.48, -9.22) * mm, "end": v(31.45, -9.32) * mm});
            skArc(sketch, "E12.43.0", {"start": v(31.1, -6.6) * mm, "mid": v(31.57, -6.5) * mm, "end": v(32.04, -6.38) * mm});
            skArc(sketch, "E12.43.1", {"start": v(31.4, -4.99) * mm, "mid": v(31.8, -5.24) * mm, "end": v(32.2, -5.52) * mm});
            skLineSegment(sketch, "E12.43.2", {"start": v(31.32, -4.96) * mm, "end": v(30.3, -4.77) * mm});
            skLineSegment(sketch, "E12.43.3", {"start": v(31.01, -6.6) * mm, "end": v(30, -6.4) * mm});
            skPoint(sketch, "E12.43.4", {"position": v(31.06, -6.6) * mm});
            skPoint(sketch, "E12.43.5", {"position": v(32.19, -6.34) * mm});
            skPoint(sketch, "E12.43.6", {"position": v(32.32, -5.62) * mm});
            skPoint(sketch, "E12.43.7", {"position": v(31.36, -4.97) * mm});
            skArc(sketch, "E12.43.8", {"start": v(32.04, -6.38) * mm, "mid": v(32.15, -6.3) * mm, "end": v(32.22, -6.18) * mm});
            skArc(sketch, "E12.43.9", {"start": v(32.3, -5.77) * mm, "mid": v(32.28, -5.63) * mm, "end": v(32.2, -5.52) * mm});
            skArc(sketch, "E12.43.10", {"start": v(32.22, -6.18) * mm, "mid": v(32.24, -6.08) * mm, "end": v(32.25, -5.98) * mm});
            skArc(sketch, "E12.43.11", {"start": v(31.01, -6.6) * mm, "mid": v(31.06, -6.6) * mm, "end": v(31.1, -6.6) * mm});
            skArc(sketch, "E12.43.12", {"start": v(31.4, -4.99) * mm, "mid": v(31.36, -4.97) * mm, "end": v(31.32, -4.96) * mm});
            skArc(sketch, "E12.43.13", {"start": v(32.3, -5.77) * mm, "mid": v(32.27, -5.87) * mm, "end": v(32.25, -5.98) * mm});
            skArc(sketch, "E12.44.0", {"start": v(31.62, -3.3) * mm, "mid": v(32.08, -3.17) * mm, "end": v(32.53, -3) * mm});
            skArc(sketch, "E12.44.1", {"start": v(31.75, -1.68) * mm, "mid": v(32.18, -1.9) * mm, "end": v(32.6, -2.13) * mm});
            skLineSegment(sketch, "E12.44.2", {"start": v(31.66, -1.66) * mm, "end": v(30.64, -1.58) * mm});
            skLineSegment(sketch, "E12.44.3", {"start": v(31.53, -3.32) * mm, "end": v(30.51, -3.24) * mm});
            skPoint(sketch, "E12.44.4", {"position": v(31.58, -3.32) * mm});
            skPoint(sketch, "E12.44.5", {"position": v(32.67, -2.94) * mm});
            skPoint(sketch, "E12.44.6", {"position": v(32.73, -2.21) * mm});
            skPoint(sketch, "E12.44.7", {"position": v(31.7, -1.66) * mm});
            skArc(sketch, "E12.44.8", {"start": v(32.53, -3) * mm, "mid": v(32.64, -2.91) * mm, "end": v(32.69, -2.78) * mm});
            skArc(sketch, "E12.44.9", {"start": v(32.72, -2.36) * mm, "mid": v(32.7, -2.23) * mm, "end": v(32.6, -2.13) * mm});
            skArc(sketch, "E12.44.10", {"start": v(32.69, -2.78) * mm, "mid": v(32.7, -2.68) * mm, "end": v(32.7, -2.57) * mm});
            skArc(sketch, "E12.44.11", {"start": v(31.53, -3.32) * mm, "mid": v(31.58, -3.31) * mm, "end": v(31.62, -3.3) * mm});
            skArc(sketch, "E12.44.12", {"start": v(31.75, -1.68) * mm, "mid": v(31.7, -1.67) * mm, "end": v(31.66, -1.66) * mm});
            skArc(sketch, "E12.44.13", {"start": v(32.72, -2.36) * mm, "mid": v(32.71, -2.47) * mm, "end": v(32.7, -2.57) * mm});
            skArc(sketch, "E12.45.0", {"start": v(31.8, 0.02) * mm, "mid": v(32.23, 0.2) * mm, "end": v(32.66, 0.42) * mm});
            skArc(sketch, "E12.45.1", {"start": v(31.75, 1.65) * mm, "mid": v(32.2, 1.48) * mm, "end": v(32.64, 1.3) * mm});
            skLineSegment(sketch, "E12.45.2", {"start": v(31.66, 1.66) * mm, "end": v(30.64, 1.63) * mm});
            skLineSegment(sketch, "E12.45.3", {"start": v(31.7, 0) * mm, "end": v(30.68, -0.03) * mm});
            skPoint(sketch, "E12.45.4", {"position": v(31.75, 0) * mm});
            skPoint(sketch, "E12.45.5", {"position": v(32.8, 0.5) * mm});
            skPoint(sketch, "E12.45.6", {"position": v(32.78, 1.22) * mm});
            skPoint(sketch, "E12.45.7", {"position": v(31.7, 1.66) * mm});
            skArc(sketch, "E12.45.8", {"start": v(32.66, 0.42) * mm, "mid": v(32.76, 0.52) * mm, "end": v(32.8, 0.65) * mm});
            skArc(sketch, "E12.45.9", {"start": v(32.79, 1.07) * mm, "mid": v(32.75, 1.2) * mm, "end": v(32.64, 1.3) * mm});
            skArc(sketch, "E12.45.10", {"start": v(32.8, 0.65) * mm, "mid": v(32.8, 0.75) * mm, "end": v(32.8, 0.86) * mm});
            skArc(sketch, "E12.45.11", {"start": v(31.7, 0) * mm, "mid": v(31.75, 0) * mm, "end": v(31.8, 0.02) * mm});
            skArc(sketch, "E12.45.12", {"start": v(31.75, 1.65) * mm, "mid": v(31.7, 1.66) * mm, "end": v(31.66, 1.66) * mm});
            skArc(sketch, "E12.45.13", {"start": v(32.79, 1.07) * mm, "mid": v(32.79, 0.96) * mm, "end": v(32.8, 0.86) * mm});
            skArc(sketch, "E12.46.0", {"start": v(31.62, 3.34) * mm, "mid": v(32.04, 3.57) * mm, "end": v(32.44, 3.83) * mm});
            skArc(sketch, "E12.46.1", {"start": v(31.4, 4.96) * mm, "mid": v(31.87, 4.84) * mm, "end": v(32.33, 4.7) * mm});
            skLineSegment(sketch, "E12.46.2", {"start": v(31.32, 4.96) * mm, "end": v(30.3, 4.83) * mm});
            skLineSegment(sketch, "E12.46.3", {"start": v(31.53, 3.31) * mm, "end": v(30.52, 3.18) * mm});
            skPoint(sketch, "E12.46.4", {"position": v(31.58, 3.32) * mm});
            skPoint(sketch, "E12.46.5", {"position": v(32.57, 3.92) * mm});
            skPoint(sketch, "E12.46.6", {"position": v(32.47, 4.64) * mm});
            skPoint(sketch, "E12.46.7", {"position": v(31.36, 4.97) * mm});
            skArc(sketch, "E12.46.8", {"start": v(32.44, 3.83) * mm, "mid": v(32.53, 3.94) * mm, "end": v(32.55, 4.07) * mm});
            skArc(sketch, "E12.46.9", {"start": v(32.5, 4.5) * mm, "mid": v(32.44, 4.62) * mm, "end": v(32.33, 4.7) * mm});
            skArc(sketch, "E12.46.10", {"start": v(32.55, 4.07) * mm, "mid": v(32.54, 4.18) * mm, "end": v(32.52, 4.28) * mm});
            skArc(sketch, "E12.46.11", {"start": v(31.53, 3.31) * mm, "mid": v(31.58, 3.32) * mm, "end": v(31.62, 3.34) * mm});
            skArc(sketch, "E12.46.12", {"start": v(31.4, 4.96) * mm, "mid": v(31.36, 4.96) * mm, "end": v(31.32, 4.96) * mm});
            skArc(sketch, "E12.46.13", {"start": v(32.5, 4.5) * mm, "mid": v(32.5, 4.39) * mm, "end": v(32.52, 4.28) * mm});
            skArc(sketch, "E12.47.0", {"start": v(31.1, 6.63) * mm, "mid": v(31.49, 6.9) * mm, "end": v(31.86, 7.2) * mm});
            skArc(sketch, "E12.47.1", {"start": v(30.71, 8.21) * mm, "mid": v(31.19, 8.14) * mm, "end": v(31.66, 8.05) * mm});
            skLineSegment(sketch, "E12.47.2", {"start": v(30.63, 8.2) * mm, "end": v(29.63, 7.97) * mm});
            skLineSegment(sketch, "E12.47.3", {"start": v(31.01, 6.6) * mm, "end": v(30.02, 6.35) * mm});
            skPoint(sketch, "E12.47.4", {"position": v(31.06, 6.6) * mm});
            skPoint(sketch, "E12.47.5", {"position": v(31.98, 7.3) * mm});
            skPoint(sketch, "E12.47.6", {"position": v(31.81, 8.01) * mm});
            skPoint(sketch, "E12.47.7", {"position": v(30.67, 8.22) * mm});
            skArc(sketch, "E12.47.8", {"start": v(31.86, 7.2) * mm, "mid": v(31.94, 7.32) * mm, "end": v(31.95, 7.45) * mm});
            skArc(sketch, "E12.47.9", {"start": v(31.85, 7.86) * mm, "mid": v(31.78, 7.98) * mm, "end": v(31.66, 8.05) * mm});
            skArc(sketch, "E12.47.10", {"start": v(31.95, 7.45) * mm, "mid": v(31.92, 7.56) * mm, "end": v(31.9, 7.66) * mm});
            skArc(sketch, "E12.47.11", {"start": v(31.01, 6.6) * mm, "mid": v(31.06, 6.6) * mm, "end": v(31.1, 6.63) * mm});
            skArc(sketch, "E12.47.12", {"start": v(30.71, 8.21) * mm, "mid": v(30.67, 8.21) * mm, "end": v(30.63, 8.2) * mm});
            skArc(sketch, "E12.47.13", {"start": v(31.85, 7.86) * mm, "mid": v(31.87, 7.76) * mm, "end": v(31.9, 7.66) * mm});
            skArc(sketch, "E12.48.0", {"start": v(30.23, 9.84) * mm, "mid": v(30.6, 10.16) * mm, "end": v(30.94, 10.5) * mm});
            skArc(sketch, "E12.48.1", {"start": v(29.69, 11.38) * mm, "mid": v(30.17, 11.36) * mm, "end": v(30.65, 11.31) * mm});
            skLineSegment(sketch, "E12.48.2", {"start": v(29.6, 11.36) * mm, "end": v(28.64, 11.02) * mm});
            skLineSegment(sketch, "E12.48.3", {"start": v(30.15, 9.8) * mm, "end": v(29.2, 9.46) * mm});
            skPoint(sketch, "E12.48.4", {"position": v(30.2, 9.81) * mm});
            skPoint(sketch, "E12.48.5", {"position": v(31.04, 10.6) * mm});
            skPoint(sketch, "E12.48.6", {"position": v(30.8, 11.3) * mm});
            skPoint(sketch, "E12.48.7", {"position": v(29.64, 11.38) * mm});
            skArc(sketch, "E12.48.8", {"start": v(30.94, 10.5) * mm, "mid": v(31, 10.61) * mm, "end": v(31, 10.75) * mm});
            skArc(sketch, "E12.48.9", {"start": v(30.85, 11.15) * mm, "mid": v(30.77, 11.26) * mm, "end": v(30.65, 11.31) * mm});
            skArc(sketch, "E12.48.10", {"start": v(31, 10.75) * mm, "mid": v(30.96, 10.85) * mm, "end": v(30.92, 10.95) * mm});
            skArc(sketch, "E12.48.11", {"start": v(30.15, 9.8) * mm, "mid": v(30.2, 9.81) * mm, "end": v(30.23, 9.84) * mm});
            skArc(sketch, "E12.48.12", {"start": v(29.69, 11.38) * mm, "mid": v(29.64, 11.37) * mm, "end": v(29.6, 11.36) * mm});
            skArc(sketch, "E12.48.13", {"start": v(30.85, 11.15) * mm, "mid": v(30.89, 11.05) * mm, "end": v(30.92, 10.95) * mm});
            skArc(sketch, "E12.49.0", {"start": v(29.04, 12.95) * mm, "mid": v(29.36, 13.3) * mm, "end": v(29.67, 13.67) * mm});
            skArc(sketch, "E12.49.1", {"start": v(28.33, 14.42) * mm, "mid": v(28.81, 14.45) * mm, "end": v(29.3, 14.46) * mm});
            skLineSegment(sketch, "E12.49.2", {"start": v(28.25, 14.4) * mm, "end": v(27.33, 13.95) * mm});
            skLineSegment(sketch, "E12.49.3", {"start": v(28.97, 12.9) * mm, "end": v(28.04, 12.45) * mm});
            skPoint(sketch, "E12.49.4", {"position": v(29, 12.91) * mm});
            skPoint(sketch, "E12.49.5", {"position": v(29.76, 13.8) * mm});
            skPoint(sketch, "E12.49.6", {"position": v(29.45, 14.45) * mm});
            skPoint(sketch, "E12.49.7", {"position": v(28.29, 14.41) * mm});
            skArc(sketch, "E12.49.8", {"start": v(29.67, 13.67) * mm, "mid": v(29.72, 13.8) * mm, "end": v(29.7, 13.93) * mm});
            skArc(sketch, "E12.49.9", {"start": v(29.52, 14.31) * mm, "mid": v(29.43, 14.41) * mm, "end": v(29.3, 14.46) * mm});
            skArc(sketch, "E12.49.10", {"start": v(29.7, 13.93) * mm, "mid": v(29.65, 14.03) * mm, "end": v(29.6, 14.12) * mm});
            skArc(sketch, "E12.49.11", {"start": v(28.97, 12.9) * mm, "mid": v(29, 12.92) * mm, "end": v(29.04, 12.95) * mm});
            skArc(sketch, "E12.49.12", {"start": v(28.33, 14.42) * mm, "mid": v(28.3, 14.41) * mm, "end": v(28.25, 14.4) * mm});
            skArc(sketch, "E12.49.13", {"start": v(29.52, 14.31) * mm, "mid": v(29.56, 14.22) * mm, "end": v(29.6, 14.12) * mm});
            skArc(sketch, "E12.50.0", {"start": v(27.52, 15.9) * mm, "mid": v(27.81, 16.3) * mm, "end": v(28.08, 16.7) * mm});
            skArc(sketch, "E12.50.1", {"start": v(26.67, 17.3) * mm, "mid": v(27.15, 17.38) * mm, "end": v(27.62, 17.44) * mm});
            skLineSegment(sketch, "E12.50.2", {"start": v(26.6, 17.27) * mm, "end": v(25.72, 16.73) * mm});
            skLineSegment(sketch, "E12.50.3", {"start": v(27.46, 15.85) * mm, "end": v(26.59, 15.32) * mm});
            skPoint(sketch, "E12.50.4", {"position": v(27.5, 15.88) * mm});
            skPoint(sketch, "E12.50.5", {"position": v(28.16, 16.83) * mm});
            skPoint(sketch, "E12.50.6", {"position": v(27.78, 17.45) * mm});
            skPoint(sketch, "E12.50.7", {"position": v(26.63, 17.3) * mm});
            skArc(sketch, "E12.50.8", {"start": v(28.08, 16.7) * mm, "mid": v(28.12, 16.83) * mm, "end": v(28.08, 16.96) * mm});
            skArc(sketch, "E12.50.9", {"start": v(27.86, 17.32) * mm, "mid": v(27.76, 17.41) * mm, "end": v(27.62, 17.44) * mm});
            skArc(sketch, "E12.50.10", {"start": v(28.08, 16.96) * mm, "mid": v(28.02, 17.05) * mm, "end": v(27.97, 17.14) * mm});
            skArc(sketch, "E12.50.11", {"start": v(27.46, 15.85) * mm, "mid": v(27.5, 15.88) * mm, "end": v(27.52, 15.9) * mm});
            skArc(sketch, "E12.50.12", {"start": v(26.67, 17.3) * mm, "mid": v(26.63, 17.29) * mm, "end": v(26.6, 17.27) * mm});
            skArc(sketch, "E12.50.13", {"start": v(27.86, 17.32) * mm, "mid": v(27.92, 17.23) * mm, "end": v(27.97, 17.14) * mm});
            skArc(sketch, "E12.51.0", {"start": v(25.71, 18.7) * mm, "mid": v(25.96, 19.11) * mm, "end": v(26.18, 19.54) * mm});
            skArc(sketch, "E12.51.1", {"start": v(24.72, 20) * mm, "mid": v(25.18, 20.13) * mm, "end": v(25.65, 20.23) * mm});
            skLineSegment(sketch, "E12.51.2", {"start": v(24.64, 19.95) * mm, "end": v(23.83, 19.33) * mm});
            skLineSegment(sketch, "E12.51.3", {"start": v(25.65, 18.64) * mm, "end": v(24.84, 18.01) * mm});
            skPoint(sketch, "E12.51.4", {"position": v(25.69, 18.66) * mm});
            skPoint(sketch, "E12.51.5", {"position": v(26.25, 19.68) * mm});
            skPoint(sketch, "E12.51.6", {"position": v(25.8, 20.26) * mm});
            skPoint(sketch, "E12.51.7", {"position": v(24.67, 19.98) * mm});
            skArc(sketch, "E12.51.8", {"start": v(26.18, 19.54) * mm, "mid": v(26.2, 19.67) * mm, "end": v(26.15, 19.8) * mm});
            skArc(sketch, "E12.51.9", {"start": v(25.9, 20.14) * mm, "mid": v(25.79, 20.22) * mm, "end": v(25.65, 20.23) * mm});
            skArc(sketch, "E12.51.10", {"start": v(26.15, 19.8) * mm, "mid": v(26.09, 19.89) * mm, "end": v(26.03, 19.97) * mm});
            skArc(sketch, "E12.51.11", {"start": v(25.65, 18.64) * mm, "mid": v(25.68, 18.67) * mm, "end": v(25.71, 18.7) * mm});
            skArc(sketch, "E12.51.12", {"start": v(24.72, 20) * mm, "mid": v(24.68, 19.98) * mm, "end": v(24.64, 19.95) * mm});
            skArc(sketch, "E12.51.13", {"start": v(25.9, 20.14) * mm, "mid": v(25.96, 20.05) * mm, "end": v(26.03, 19.97) * mm});
            skArc(sketch, "E12.52.0", {"start": v(23.62, 21.28) * mm, "mid": v(23.82, 21.72) * mm, "end": v(24, 22.17) * mm});
            skArc(sketch, "E12.52.1", {"start": v(22.5, 22.47) * mm, "mid": v(22.94, 22.65) * mm, "end": v(23.4, 22.8) * mm});
            skLineSegment(sketch, "E12.52.2", {"start": v(22.42, 22.42) * mm, "end": v(21.68, 21.72) * mm});
            skLineSegment(sketch, "E12.52.3", {"start": v(23.56, 21.21) * mm, "end": v(22.82, 20.51) * mm});
            skPoint(sketch, "E12.52.4", {"position": v(23.6, 21.24) * mm});
            skPoint(sketch, "E12.52.5", {"position": v(24.04, 22.32) * mm});
            skPoint(sketch, "E12.52.6", {"position": v(23.54, 22.84) * mm});
            skPoint(sketch, "E12.52.7", {"position": v(22.45, 22.45) * mm});
            skArc(sketch, "E12.52.8", {"start": v(24, 22.17) * mm, "mid": v(24, 22.3) * mm, "end": v(23.94, 22.43) * mm});
            skArc(sketch, "E12.52.9", {"start": v(23.65, 22.73) * mm, "mid": v(23.53, 22.8) * mm, "end": v(23.4, 22.8) * mm});
            skArc(sketch, "E12.52.10", {"start": v(23.94, 22.43) * mm, "mid": v(23.87, 22.5) * mm, "end": v(23.8, 22.58) * mm});
            skArc(sketch, "E12.52.11", {"start": v(23.56, 21.21) * mm, "mid": v(23.6, 21.25) * mm, "end": v(23.62, 21.28) * mm});
            skArc(sketch, "E12.52.12", {"start": v(22.5, 22.47) * mm, "mid": v(22.45, 22.45) * mm, "end": v(22.42, 22.42) * mm});
            skArc(sketch, "E12.52.13", {"start": v(23.65, 22.73) * mm, "mid": v(23.72, 22.66) * mm, "end": v(23.8, 22.58) * mm});
            skArc(sketch, "E12.53.0", {"start": v(21.26, 23.64) * mm, "mid": v(21.42, 24.1) * mm, "end": v(21.54, 24.56) * mm});
            skArc(sketch, "E12.53.1", {"start": v(20.02, 24.7) * mm, "mid": v(20.44, 24.92) * mm, "end": v(20.88, 25.12) * mm});
            skLineSegment(sketch, "E12.53.2", {"start": v(19.95, 24.64) * mm, "end": v(19.29, 23.86) * mm});
            skLineSegment(sketch, "E12.53.3", {"start": v(21.22, 23.56) * mm, "end": v(20.55, 22.78) * mm});
            skPoint(sketch, "E12.53.4", {"position": v(21.24, 23.6) * mm});
            skPoint(sketch, "E12.53.5", {"position": v(21.58, 24.7) * mm});
            skPoint(sketch, "E12.53.6", {"position": v(21.03, 25.18) * mm});
            skPoint(sketch, "E12.53.7", {"position": v(19.98, 24.67) * mm});
            skArc(sketch, "E12.53.8", {"start": v(21.54, 24.56) * mm, "mid": v(21.54, 24.7) * mm, "end": v(21.46, 24.8) * mm});
            skArc(sketch, "E12.53.9", {"start": v(21.14, 25.08) * mm, "mid": v(21.02, 25.14) * mm, "end": v(20.88, 25.12) * mm});
            skArc(sketch, "E12.53.10", {"start": v(21.46, 24.8) * mm, "mid": v(21.38, 24.88) * mm, "end": v(21.3, 24.94) * mm});
            skArc(sketch, "E12.53.11", {"start": v(21.22, 23.56) * mm, "mid": v(21.24, 23.6) * mm, "end": v(21.26, 23.64) * mm});
            skArc(sketch, "E12.53.12", {"start": v(20.02, 24.7) * mm, "mid": v(19.98, 24.67) * mm, "end": v(19.95, 24.64) * mm});
            skArc(sketch, "E12.53.13", {"start": v(21.14, 25.08) * mm, "mid": v(21.22, 25.01) * mm, "end": v(21.3, 24.94) * mm});
            skArc(sketch, "E12.54.0", {"start": v(18.67, 25.73) * mm, "mid": v(18.78, 26.2) * mm, "end": v(18.86, 26.67) * mm});
            skArc(sketch, "E12.54.1", {"start": v(17.33, 26.65) * mm, "mid": v(17.73, 26.92) * mm, "end": v(18.14, 27.17) * mm});
            skLineSegment(sketch, "E12.54.2", {"start": v(17.27, 26.6) * mm, "end": v(16.69, 25.75) * mm});
            skLineSegment(sketch, "E12.54.3", {"start": v(18.64, 25.65) * mm, "end": v(18.06, 24.8) * mm});
            skPoint(sketch, "E12.54.4", {"position": v(18.66, 25.69) * mm});
            skPoint(sketch, "E12.54.5", {"position": v(18.88, 26.83) * mm});
            skPoint(sketch, "E12.54.6", {"position": v(18.28, 27.24) * mm});
            skPoint(sketch, "E12.54.7", {"position": v(17.3, 26.63) * mm});
            skArc(sketch, "E12.54.8", {"start": v(18.86, 26.67) * mm, "mid": v(18.84, 26.8) * mm, "end": v(18.75, 26.92) * mm});
            skArc(sketch, "E12.54.9", {"start": v(18.4, 27.15) * mm, "mid": v(18.28, 27.2) * mm, "end": v(18.14, 27.17) * mm});
            skArc(sketch, "E12.54.10", {"start": v(18.75, 26.92) * mm, "mid": v(18.67, 26.98) * mm, "end": v(18.58, 27.03) * mm});
            skArc(sketch, "E12.54.11", {"start": v(18.64, 25.65) * mm, "mid": v(18.66, 25.69) * mm, "end": v(18.67, 25.73) * mm});
            skArc(sketch, "E12.54.12", {"start": v(17.33, 26.65) * mm, "mid": v(17.3, 26.63) * mm, "end": v(17.27, 26.6) * mm});
            skArc(sketch, "E12.54.13", {"start": v(18.4, 27.15) * mm, "mid": v(18.5, 27.1) * mm, "end": v(18.58, 27.03) * mm});
            skArc(sketch, "E12.55.0", {"start": v(15.88, 27.54) * mm, "mid": v(15.94, 28.02) * mm, "end": v(15.97, 28.5) * mm});
            skArc(sketch, "E12.55.1", {"start": v(14.45, 28.32) * mm, "mid": v(14.82, 28.63) * mm, "end": v(15.2, 28.91) * mm});
            skLineSegment(sketch, "E12.55.2", {"start": v(14.4, 28.25) * mm, "end": v(13.9, 27.35) * mm});
            skLineSegment(sketch, "E12.55.3", {"start": v(15.85, 27.46) * mm, "end": v(15.37, 26.56) * mm});
            skPoint(sketch, "E12.55.4", {"position": v(15.87, 27.5) * mm});
            skPoint(sketch, "E12.55.5", {"position": v(15.97, 28.65) * mm});
            skPoint(sketch, "E12.55.6", {"position": v(15.33, 29) * mm});
            skPoint(sketch, "E12.55.7", {"position": v(14.41, 28.29) * mm});
            skArc(sketch, "E12.55.8", {"start": v(15.97, 28.5) * mm, "mid": v(15.94, 28.63) * mm, "end": v(15.84, 28.73) * mm});
            skArc(sketch, "E12.55.9", {"start": v(15.47, 28.93) * mm, "mid": v(15.33, 28.96) * mm, "end": v(15.2, 28.91) * mm});
            skArc(sketch, "E12.55.10", {"start": v(15.84, 28.73) * mm, "mid": v(15.75, 28.78) * mm, "end": v(15.65, 28.83) * mm});
            skArc(sketch, "E12.55.11", {"start": v(15.85, 27.46) * mm, "mid": v(15.87, 27.5) * mm, "end": v(15.88, 27.54) * mm});
            skArc(sketch, "E12.55.12", {"start": v(14.45, 28.32) * mm, "mid": v(14.42, 28.29) * mm, "end": v(14.4, 28.25) * mm});
            skArc(sketch, "E12.55.13", {"start": v(15.47, 28.93) * mm, "mid": v(15.56, 28.88) * mm, "end": v(15.65, 28.83) * mm});
            skArc(sketch, "E12.56.0", {"start": v(12.92, 29.05) * mm, "mid": v(12.92, 29.53) * mm, "end": v(12.9, 30.01) * mm});
            skArc(sketch, "E12.56.1", {"start": v(11.4, 29.67) * mm, "mid": v(11.74, 30.02) * mm, "end": v(12.1, 30.34) * mm});
            skLineSegment(sketch, "E12.56.2", {"start": v(11.36, 29.6) * mm, "end": v(10.97, 28.66) * mm});
            skLineSegment(sketch, "E12.56.3", {"start": v(12.9, 28.96) * mm, "end": v(12.5, 28.02) * mm});
            skPoint(sketch, "E12.56.4", {"position": v(12.91, 29) * mm});
            skPoint(sketch, "E12.56.5", {"position": v(12.89, 30.17) * mm});
            skPoint(sketch, "E12.56.6", {"position": v(12.22, 30.44) * mm});
            skPoint(sketch, "E12.56.7", {"position": v(11.38, 29.64) * mm});
            skArc(sketch, "E12.56.8", {"start": v(12.9, 30.01) * mm, "mid": v(12.86, 30.14) * mm, "end": v(12.75, 30.23) * mm});
            skArc(sketch, "E12.56.9", {"start": v(12.36, 30.39) * mm, "mid": v(12.22, 30.4) * mm, "end": v(12.1, 30.34) * mm});
            skArc(sketch, "E12.56.10", {"start": v(12.75, 30.23) * mm, "mid": v(12.65, 30.27) * mm, "end": v(12.55, 30.3) * mm});
            skArc(sketch, "E12.56.11", {"start": v(12.9, 28.96) * mm, "mid": v(12.91, 29) * mm, "end": v(12.92, 29.05) * mm});
            skArc(sketch, "E12.56.12", {"start": v(11.4, 29.67) * mm, "mid": v(11.38, 29.64) * mm, "end": v(11.36, 29.6) * mm});
            skArc(sketch, "E12.56.13", {"start": v(12.36, 30.39) * mm, "mid": v(12.46, 30.35) * mm, "end": v(12.55, 30.3) * mm});
            skArc(sketch, "E12.57.0", {"start": v(9.8, 30.24) * mm, "mid": v(9.77, 30.72) * mm, "end": v(9.7, 31.2) * mm});
            skArc(sketch, "E12.57.1", {"start": v(8.24, 30.7) * mm, "mid": v(8.54, 31.08) * mm, "end": v(8.86, 31.44) * mm});
            skLineSegment(sketch, "E12.57.2", {"start": v(8.2, 30.63) * mm, "end": v(7.91, 29.64) * mm});
            skLineSegment(sketch, "E12.57.3", {"start": v(9.8, 30.15) * mm, "end": v(9.5, 29.17) * mm});
            skPoint(sketch, "E12.57.4", {"position": v(9.81, 30.2) * mm});
            skPoint(sketch, "E12.57.5", {"position": v(9.67, 31.35) * mm});
            skPoint(sketch, "E12.57.6", {"position": v(8.97, 31.55) * mm});
            skPoint(sketch, "E12.57.7", {"position": v(8.22, 30.67) * mm});
            skArc(sketch, "E12.57.8", {"start": v(9.7, 31.2) * mm, "mid": v(9.63, 31.32) * mm, "end": v(9.52, 31.4) * mm});
            skArc(sketch, "E12.57.9", {"start": v(9.12, 31.51) * mm, "mid": v(8.98, 31.51) * mm, "end": v(8.86, 31.44) * mm});
            skArc(sketch, "E12.57.10", {"start": v(9.52, 31.4) * mm, "mid": v(9.42, 31.42) * mm, "end": v(9.32, 31.45) * mm});
            skArc(sketch, "E12.57.11", {"start": v(9.8, 30.15) * mm, "mid": v(9.8, 30.2) * mm, "end": v(9.8, 30.24) * mm});
            skArc(sketch, "E12.57.12", {"start": v(8.24, 30.7) * mm, "mid": v(8.22, 30.67) * mm, "end": v(8.2, 30.63) * mm});
            skArc(sketch, "E12.57.13", {"start": v(9.12, 31.51) * mm, "mid": v(9.22, 31.48) * mm, "end": v(9.32, 31.45) * mm});
            skArc(sketch, "E12.58.0", {"start": v(6.6, 31.1) * mm, "mid": v(6.5, 31.57) * mm, "end": v(6.38, 32.04) * mm});
            skArc(sketch, "E12.58.1", {"start": v(4.99, 31.4) * mm, "mid": v(5.24, 31.8) * mm, "end": v(5.52, 32.2) * mm});
            skLineSegment(sketch, "E12.58.2", {"start": v(4.96, 31.32) * mm, "end": v(4.77, 30.3) * mm});
            skLineSegment(sketch, "E12.58.3", {"start": v(6.6, 31.01) * mm, "end": v(6.4, 30) * mm});
            skPoint(sketch, "E12.58.4", {"position": v(6.6, 31.06) * mm});
            skPoint(sketch, "E12.58.5", {"position": v(6.34, 32.19) * mm});
            skPoint(sketch, "E12.58.6", {"position": v(5.62, 32.32) * mm});
            skPoint(sketch, "E12.58.7", {"position": v(4.97, 31.36) * mm});
            skArc(sketch, "E12.58.8", {"start": v(6.38, 32.04) * mm, "mid": v(6.3, 32.15) * mm, "end": v(6.18, 32.22) * mm});
            skArc(sketch, "E12.58.9", {"start": v(5.77, 32.3) * mm, "mid": v(5.63, 32.28) * mm, "end": v(5.52, 32.2) * mm});
            skArc(sketch, "E12.58.10", {"start": v(6.18, 32.22) * mm, "mid": v(6.08, 32.24) * mm, "end": v(5.98, 32.25) * mm});
            skArc(sketch, "E12.58.11", {"start": v(6.6, 31.01) * mm, "mid": v(6.6, 31.06) * mm, "end": v(6.6, 31.1) * mm});
            skArc(sketch, "E12.58.12", {"start": v(4.99, 31.4) * mm, "mid": v(4.97, 31.36) * mm, "end": v(4.96, 31.32) * mm});
            skArc(sketch, "E12.58.13", {"start": v(5.77, 32.3) * mm, "mid": v(5.87, 32.27) * mm, "end": v(5.98, 32.25) * mm});
            skArc(sketch, "E12.59.0", {"start": v(3.3, 31.62) * mm, "mid": v(3.17, 32.08) * mm, "end": v(3, 32.53) * mm});
            skArc(sketch, "E12.59.1", {"start": v(1.68, 31.75) * mm, "mid": v(1.9, 32.18) * mm, "end": v(2.13, 32.6) * mm});
            skLineSegment(sketch, "E12.59.2", {"start": v(1.66, 31.66) * mm, "end": v(1.58, 30.64) * mm});
            skLineSegment(sketch, "E12.59.3", {"start": v(3.32, 31.53) * mm, "end": v(3.24, 30.51) * mm});
            skPoint(sketch, "E12.59.4", {"position": v(3.32, 31.58) * mm});
            skPoint(sketch, "E12.59.5", {"position": v(2.94, 32.67) * mm});
            skPoint(sketch, "E12.59.6", {"position": v(2.21, 32.73) * mm});
            skPoint(sketch, "E12.59.7", {"position": v(1.66, 31.7) * mm});
            skArc(sketch, "E12.59.8", {"start": v(3, 32.53) * mm, "mid": v(2.91, 32.64) * mm, "end": v(2.78, 32.69) * mm});
            skArc(sketch, "E12.59.9", {"start": v(2.36, 32.72) * mm, "mid": v(2.23, 32.7) * mm, "end": v(2.13, 32.6) * mm});
            skArc(sketch, "E12.59.10", {"start": v(2.78, 32.69) * mm, "mid": v(2.68, 32.7) * mm, "end": v(2.57, 32.7) * mm});
            skArc(sketch, "E12.59.11", {"start": v(3.32, 31.53) * mm, "mid": v(3.31, 31.58) * mm, "end": v(3.3, 31.62) * mm});
            skArc(sketch, "E12.59.12", {"start": v(1.68, 31.75) * mm, "mid": v(1.67, 31.7) * mm, "end": v(1.66, 31.66) * mm});
            skArc(sketch, "E12.59.13", {"start": v(2.36, 32.72) * mm, "mid": v(2.47, 32.71) * mm, "end": v(2.57, 32.7) * mm});
            skSolve(sketch);
        }
        {
            var Q0;
            Q0 = qSketchRegion(id + "F0", true);
            var Q1;
            {var subQ0=sQuery(id+"F0.wireOp",EDGE,"E0");var subQ26=makeQuery(id+"F0.imprint","INTERSECT",VERTEX,{"derivedFrom":[subQ0,sQuery(id+"F0.wireOp",EDGE,"E12.45.2")]});Q1=makeQuery(id+"F0.imprint","IMPRINT",FACE,{"disambiguationData":[TD([[makeQuery(id+"F0.imprint","IMPRINT",EDGE,{"disambiguationData":[TD([[subQ26,-1.0]])],"derivedFrom":subQ0}),1.0]])]});}
            extrude(context, id + "F1", {"entities" : qUnion([Q0, Q1]), "depth" : 6.35 * mm});
        }
        {
            var Q0;
            Q0=qCreatedBy(makeId("Front.planeOp"),FACE);
            var sketch = newSketch(context, id + "F2", { "sketchPlane" : qUnion([Q0])});
            skCircle(sketch, "E13", {"center": v(0, 0) * mm, "radius": 5.59 * mm});
            skSolve(sketch);
        }
        {
            var Q0;
            Q0 = qSketchRegion(id + "F2", true);
            extrude(context, id + "F3", {"entities" : qUnion([Q0]), "operationType" : NewBodyOperationType.REMOVE, "depth" : 25.22 * mm});
        }
    });
